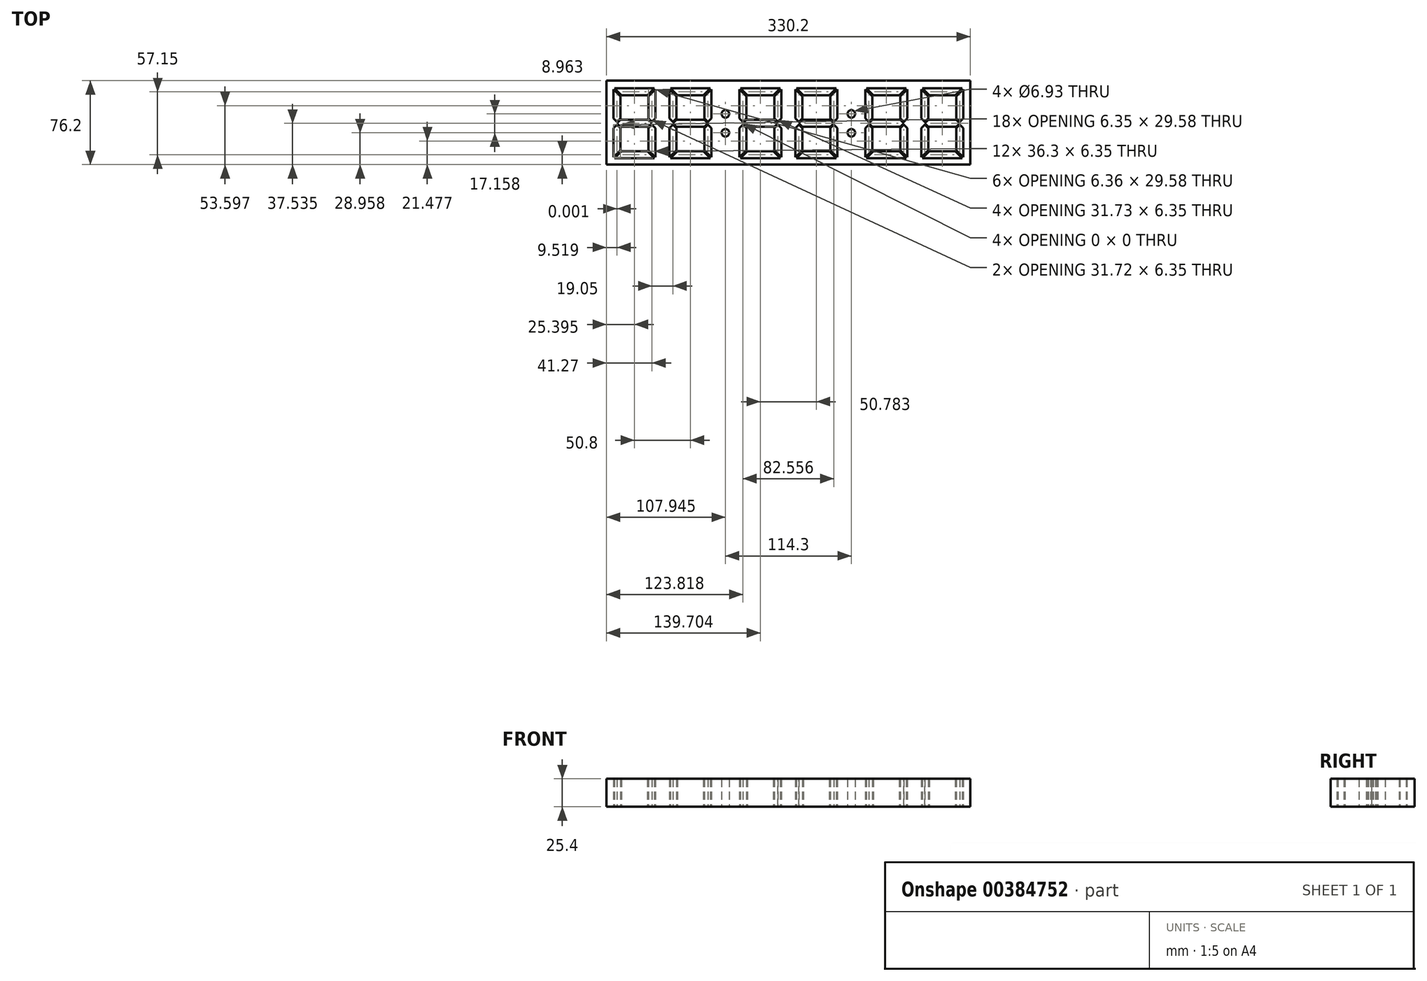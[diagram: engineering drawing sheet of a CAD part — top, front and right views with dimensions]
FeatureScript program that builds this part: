
annotation { "Feature Type Name" : "Feature", "Feature Type Description" : "" }
export const myFeature = defineFeature(function(context is Context, id is Id, definition is map)
    precondition{}
    {
        {
            var Q0;
            Q0=qCreatedBy(makeId("Top.planeOp"),FACE);
            var sketch = newSketch(context, id + "F0", { "sketchPlane" : qUnion([Q0])});
            skLineSegment(sketch, "E0.bottom", {"start": v(-71.32, 52.19) * mm, "end": v(-45.92, 52.19) * mm});
            skLineSegment(sketch, "E1.bottom", {"start": v(-64.08, 45.28) * mm, "end": v(-27.77, 45.28) * mm});
            skLineSegment(sketch, "E1.top", {"start": v(-64.08, -18.22) * mm, "end": v(-27.77, -18.22) * mm});
            skLineSegment(sketch, "E1.left", {"start": v(-64.98, 44.38) * mm, "end": v(-64.98, 18.04) * mm});
            skLineSegment(sketch, "E1.right", {"start": v(-26.87, 44.38) * mm, "end": v(-26.87, 18.04) * mm});
            skLineSegment(sketch, "E2.bottom", {"start": v(-57.73, 38.93) * mm, "end": v(-34.12, 38.93) * mm});
            skLineSegment(sketch, "E2.top", {"start": v(-57.73, -11.87) * mm, "end": v(-34.12, -11.87) * mm});
            skLineSegment(sketch, "E2.left", {"start": v(-58.62, 38.03) * mm, "end": v(-58.62, 17.97) * mm});
            skLineSegment(sketch, "E2.right", {"start": v(-33.22, 38.03) * mm, "end": v(-33.22, 17.97) * mm});
            skLineSegment(sketch, "E3", {"start": v(-45.92, 52.19) * mm, "end": v(-20.52, 52.19) * mm});
            skLineSegment(sketch, "E4", {"start": v(-61.35, 42.55) * mm, "end": v(-57.73, 38.93) * mm});
            skLineSegment(sketch, "E5", {"start": v(-62.25, 41.65) * mm, "end": v(-58.62, 38.03) * mm});
            skLineSegment(sketch, "E6", {"start": v(-62.25, 41.65) * mm, "end": v(-64.98, 44.38) * mm});
            skLineSegment(sketch, "E7", {"start": v(-61.35, 42.55) * mm, "end": v(-64.08, 45.28) * mm});
            skPoint(sketch, "E8.orphan", {"position": v(-64.98, 45.28) * mm});
            skPoint(sketch, "E9.orphan", {"position": v(-58.62, 38.93) * mm});
            skPoint(sketch, "E10.start.orphan", {"position": v(-61.8, 42.1) * mm});
            skLineSegment(sketch, "E11.MirrorCS", {"start": v(-29.6, 41.65) * mm, "end": v(-33.22, 38.03) * mm});
            skLineSegment(sketch, "E12.MirrorCS", {"start": v(-30.5, 42.55) * mm, "end": v(-34.12, 38.93) * mm});
            skPoint(sketch, "E13.MirrorP", {"position": v(-30.05, 42.1) * mm});
            skPoint(sketch, "E14.MirrorP", {"position": v(-26.87, 45.28) * mm});
            skLineSegment(sketch, "E15.MirrorCS", {"start": v(-30.5, 42.55) * mm, "end": v(-27.77, 45.28) * mm});
            skLineSegment(sketch, "E16.MirrorCS", {"start": v(-29.6, 41.65) * mm, "end": v(-26.87, 44.38) * mm});
            skPoint(sketch, "E17.MirrorP", {"position": v(-33.22, 38.93) * mm});
            skLineSegment(sketch, "E18.MirrorCS", {"start": v(-61.35, -15.5) * mm, "end": v(-57.73, -11.87) * mm});
            skPoint(sketch, "E19.MirrorP", {"position": v(-64.97, -18.22) * mm});
            skPoint(sketch, "E20.MirrorP", {"position": v(-61.8, -15.05) * mm});
            skLineSegment(sketch, "E21.MirrorCS", {"start": v(-29.6, -14.6) * mm, "end": v(-26.87, -17.32) * mm});
            skLineSegment(sketch, "E22.MirrorCS", {"start": v(-26.87, -17.32) * mm, "end": v(-26.87, 9) * mm});
            skLineSegment(sketch, "E23.MirrorCS", {"start": v(-29.6, -14.6) * mm, "end": v(-33.22, -10.97) * mm});
            skLineSegment(sketch, "E24.MirrorCS", {"start": v(-62.25, -14.6) * mm, "end": v(-64.98, -17.33) * mm});
            skPoint(sketch, "E25.MirrorP", {"position": v(-30.05, -15.05) * mm});
            skLineSegment(sketch, "E26.MirrorCS", {"start": v(-30.5, -15.5) * mm, "end": v(-27.77, -18.22) * mm});
            skPoint(sketch, "E27.MirrorP", {"position": v(-26.87, -18.22) * mm});
            skLineSegment(sketch, "E28.MirrorCS", {"start": v(-30.5, -15.5) * mm, "end": v(-34.12, -11.87) * mm});
            skPoint(sketch, "E29.MirrorP", {"position": v(-33.22, -11.87) * mm});
            skPoint(sketch, "E30.MirrorP", {"position": v(-58.62, -11.87) * mm});
            skLineSegment(sketch, "E31.MirrorCS", {"start": v(-64.98, -17.33) * mm, "end": v(-64.98, 9.01) * mm});
            skLineSegment(sketch, "E32.MirrorCS", {"start": v(-61.35, -15.5) * mm, "end": v(-64.08, -18.22) * mm});
            skPoint(sketch, "E33.MirrorCS.end.orphan", {"position": v(-42, 45.28) * mm});
            skPoint(sketch, "E33.MirrorCS.start.orphan", {"position": v(-42, 38.93) * mm});
            skPoint(sketch, "E34.end.orphan", {"position": v(-49.84, 45.28) * mm});
            skPoint(sketch, "E34.start.orphan", {"position": v(-49.84, 38.93) * mm});
            skPoint(sketch, "E35.end.orphan", {"position": v(-45.92, -24.57) * mm});
            skPoint(sketch, "E36.MirrorCS.end.orphan", {"position": v(-49.84, -18.22) * mm});
            skPoint(sketch, "E36.MirrorCS.start.orphan", {"position": v(-49.84, -11.87) * mm});
            skPoint(sketch, "E37.MirrorCS.end.orphan", {"position": v(-42, -18.22) * mm});
            skPoint(sketch, "E37.MirrorCS.start.orphan", {"position": v(-42, -11.87) * mm});
            skPoint(sketch, "E38.orphan", {"position": v(-58.62, 12.9) * mm});
            skPoint(sketch, "E39.orphan", {"position": v(-58.62, 14.16) * mm});
            skPoint(sketch, "E40.end.orphan", {"position": v(-64.97, 17.68) * mm});
            skPoint(sketch, "E41.MirrorCS.start.orphan", {"position": v(-58.3, 16.78) * mm});
            skPoint(sketch, "E42.MirrorCS.end.orphan", {"position": v(-64.97, 13.53) * mm});
            skPoint(sketch, "E43.MirrorP", {"position": v(-58.3, 10.28) * mm});
            skPoint(sketch, "E44.end.orphan", {"position": v(-64.98, 13.53) * mm});
            skLineSegment(sketch, "E45.trimOffspring", {"start": v(-64.98, 9.01) * mm, "end": v(-64.98, -17.33) * mm});
            skLineSegment(sketch, "E46.trimOffspring", {"start": v(-58.63, 9.08) * mm, "end": v(-58.63, -10.98) * mm});
            skPoint(sketch, "E47.trimOffspring.start.orphan", {"position": v(-64.97, 16.77) * mm});
            skPoint(sketch, "E48.trimOffspring.end.orphan", {"position": v(-26.87, 13.53) * mm});
            skLineSegment(sketch, "E49.MirrorCS", {"start": v(-26.87, 9) * mm, "end": v(-26.87, -17.32) * mm});
            skPoint(sketch, "E50.MirrorP", {"position": v(-33.54, 10.28) * mm});
            skPoint(sketch, "E51.MirrorP", {"position": v(-33.22, 12.9) * mm});
            skPoint(sketch, "E52.MirrorP", {"position": v(-33.54, 16.78) * mm});
            skLineSegment(sketch, "E53.MirrorCS", {"start": v(-26.87, -17.5) * mm, "end": v(-26.87, 9) * mm});
            skLineSegment(sketch, "E54.MirrorCS", {"start": v(-33.22, 9.08) * mm, "end": v(-33.22, -10.97) * mm});
            skPoint(sketch, "E55.MirrorP", {"position": v(-26.87, 16.77) * mm});
            skPoint(sketch, "E56.MirrorP", {"position": v(-26.87, 17.68) * mm});
            skPoint(sketch, "E57.MirrorP", {"position": v(-33.22, 14.16) * mm});
            skPoint(sketch, "E58.orphan", {"position": v(-64.98, -18.22) * mm});
            skLineSegment(sketch, "E59", {"start": v(-62.25, -14.6) * mm, "end": v(-58.63, -10.98) * mm});
            skLineSegment(sketch, "E60", {"start": v(-58.62, 16.7) * mm, "end": v(-61.78, 13.54) * mm});
            skPoint(sketch, "E61.trimOffspring.end.orphan", {"position": v(-58.62, 13.97) * mm});
            skPoint(sketch, "E62.right.start.orphan", {"position": v(-58.62, 13.53) * mm});
            skPoint(sketch, "E63.trimOffspring.end.orphan", {"position": v(-71.32, 13.8) * mm});
            skPoint(sketch, "E64.orphan", {"position": v(-61.8, 16.7) * mm});
            skLineSegment(sketch, "E65", {"start": v(-61.77, 14.8) * mm, "end": v(-58.62, 17.97) * mm});
            skLineSegment(sketch, "E66.MirrorCS", {"start": v(-61.77, 14.8) * mm, "end": v(-64.9, 17.97) * mm});
            skPoint(sketch, "E67.MirrorP", {"position": v(-61.8, 10.35) * mm});
            skLineSegment(sketch, "E68.MirrorCS", {"start": v(-61.77, 12.25) * mm, "end": v(-58.63, 9.08) * mm});
            skLineSegment(sketch, "E69.MirrorCS", {"start": v(-61.77, 12.25) * mm, "end": v(-64.9, 9.08) * mm});
            skLineSegment(sketch, "E70", {"start": v(-58.62, 16.7) * mm, "end": v(-33.22, 16.7) * mm});
            skLineSegment(sketch, "E71", {"start": v(-58.63, 10.35) * mm, "end": v(-33.23, 10.35) * mm});
            skLineSegment(sketch, "E72", {"start": v(-61.78, 13.54) * mm, "end": v(-58.63, 10.35) * mm});
            skLineSegment(sketch, "E73", {"start": v(-64.9, 17.97) * mm, "end": v(-64.98, 18.04) * mm});
            skPoint(sketch, "E74.orphan", {"position": v(-64.98, 17.1) * mm});
            skPoint(sketch, "E75.end.orphan", {"position": v(-64.97, 16.7) * mm});
            skPoint(sketch, "E76.trimOffspring.end.orphan", {"position": v(-58.63, 9.96) * mm});
            skLineSegment(sketch, "E77", {"start": v(-64.9, 9.08) * mm, "end": v(-64.98, 9.01) * mm});
            skPoint(sketch, "E78.orphan", {"position": v(-64.98, 9.96) * mm});
            skLineSegment(sketch, "E79.MirrorCS", {"start": v(-30.08, 14.8) * mm, "end": v(-33.22, 17.97) * mm});
            skLineSegment(sketch, "E80.MirrorCS", {"start": v(-30.08, 14.8) * mm, "end": v(-26.94, 17.97) * mm});
            skLineSegment(sketch, "E81.MirrorCS", {"start": v(-33.22, 16.7) * mm, "end": v(-30.07, 13.54) * mm});
            skLineSegment(sketch, "E82.MirrorCS", {"start": v(-30.07, 13.54) * mm, "end": v(-33.22, 10.35) * mm});
            skLineSegment(sketch, "E83.MirrorCS", {"start": v(-30.08, 12.26) * mm, "end": v(-33.22, 9.08) * mm});
            skLineSegment(sketch, "E84.MirrorCS", {"start": v(-30.08, 12.26) * mm, "end": v(-26.94, 9.08) * mm});
            skPoint(sketch, "E85.orphan", {"position": v(-33.22, 13.53) * mm});
            skPoint(sketch, "E86.orphan", {"position": v(-33.22, 9.96) * mm});
            skLineSegment(sketch, "E87", {"start": v(-26.94, 9.08) * mm, "end": v(-26.87, 9) * mm});
            skPoint(sketch, "E88.orphan", {"position": v(-33.22, 17.1) * mm});
            skLineSegment(sketch, "E89", {"start": v(-26.94, 17.97) * mm, "end": v(-26.87, 18.04) * mm});
            skPoint(sketch, "E90.end.orphan", {"position": v(-26.87, 16.7) * mm});
            skLineSegment(sketch, "E91.bottom", {"start": v(-20.52, 52.19) * mm, "end": v(-14.17, 52.19) * mm});
            skLineSegment(sketch, "E91.top", {"start": v(-20.52, -24.01) * mm, "end": v(-7.82, -24.01) * mm});
            skLineSegment(sketch, "E92", {"start": v(-14.17, 52.19) * mm, "end": v(-7.82, 52.19) * mm});
            skCircle(sketch, "E93", {"center": v(-14.17, 22.1) * mm, "radius": 3.46 * mm});
            skPoint(sketch, "E94.orphan", {"position": v(-14.17, 52.19) * mm});
            skPoint(sketch, "E95.trimOffspring.end.orphan", {"position": v(-14.17, -24.01) * mm});
            skCircle(sketch, "E96.MirrorC", {"center": v(-14.17, 4.95) * mm, "radius": 3.46 * mm});
            skPoint(sketch, "E97.end.orphan", {"position": v(-7.82, 14.09) * mm});
            skPoint(sketch, "E98.end.orphan", {"position": v(-20.52, -24.57) * mm});
            skPoint(sketch, "E98.start.orphan", {"position": v(-20.52, 13.53) * mm});
            skPoint(sketch, "E99.start.orphan", {"position": v(-20.52, 13.8) * mm});
            skPoint(sketch, "E100.MirrorP", {"position": v(-77.67, 13.53) * mm});
            skPoint(sketch, "E101.MirrorP", {"position": v(-115.77, 13.53) * mm});
            skLineSegment(sketch, "E102.MirrorCS", {"start": v(-77.74, 9.08) * mm, "end": v(-77.67, 9.01) * mm});
            skLineSegment(sketch, "E103.MirrorCS", {"start": v(-115.7, 9.08) * mm, "end": v(-115.78, 9) * mm});
            skLineSegment(sketch, "E104.MirrorCS", {"start": v(-115.7, 17.97) * mm, "end": v(-115.77, 18.04) * mm});
            skLineSegment(sketch, "E105.MirrorCS", {"start": v(-109.42, 16.7) * mm, "end": v(-112.58, 13.54) * mm});
            skLineSegment(sketch, "E106.MirrorCS", {"start": v(-80.87, 13.54) * mm, "end": v(-84.02, 10.35) * mm});
            skLineSegment(sketch, "E107.MirrorCS", {"start": v(-84.03, 16.7) * mm, "end": v(-80.87, 13.54) * mm});
            skLineSegment(sketch, "E108.MirrorCS", {"start": v(-112.58, 13.54) * mm, "end": v(-109.42, 10.35) * mm});
            skLineSegment(sketch, "E109.MirrorCS", {"start": v(-77.74, 17.97) * mm, "end": v(-77.67, 18.04) * mm});
            skLineSegment(sketch, "E110.MirrorCS", {"start": v(-115.78, 9) * mm, "end": v(-115.77, -17.32) * mm});
            skLineSegment(sketch, "E111.MirrorCS", {"start": v(-80.88, 14.8) * mm, "end": v(-84.03, 17.97) * mm});
            skLineSegment(sketch, "E112.MirrorCS", {"start": v(-113.05, -14.6) * mm, "end": v(-115.77, -17.32) * mm});
            skLineSegment(sketch, "E113.MirrorCS", {"start": v(-80.88, 14.8) * mm, "end": v(-77.74, 17.97) * mm});
            skLineSegment(sketch, "E114.MirrorCS", {"start": v(-80.4, -14.6) * mm, "end": v(-77.67, -17.33) * mm});
            skLineSegment(sketch, "E115.MirrorCS", {"start": v(-80.88, 12.25) * mm, "end": v(-84.02, 9.08) * mm});
            skLineSegment(sketch, "E116.MirrorCS", {"start": v(-112.15, -15.5) * mm, "end": v(-114.88, -18.22) * mm});
            skLineSegment(sketch, "E117.MirrorCS", {"start": v(-80.88, 12.25) * mm, "end": v(-77.74, 9.08) * mm});
            skLineSegment(sketch, "E118.MirrorCS", {"start": v(-113.05, 41.65) * mm, "end": v(-115.77, 44.38) * mm});
            skLineSegment(sketch, "E119.MirrorCS", {"start": v(-81.3, -15.5) * mm, "end": v(-78.57, -18.22) * mm});
            skLineSegment(sketch, "E120.MirrorCS", {"start": v(-81.3, 42.55) * mm, "end": v(-78.57, 45.28) * mm});
            skLineSegment(sketch, "E121.MirrorCS", {"start": v(-112.57, 14.8) * mm, "end": v(-115.7, 17.97) * mm});
            skLineSegment(sketch, "E122.MirrorCS", {"start": v(-112.57, 14.8) * mm, "end": v(-109.42, 17.97) * mm});
            skLineSegment(sketch, "E123.MirrorCS", {"start": v(-112.15, 42.55) * mm, "end": v(-114.88, 45.28) * mm});
            skPoint(sketch, "E124.MirrorP", {"position": v(-84.02, 13.53) * mm});
            skLineSegment(sketch, "E125.MirrorCS", {"start": v(-109.42, 9.08) * mm, "end": v(-109.42, -10.97) * mm});
            skPoint(sketch, "E126.MirrorP", {"position": v(-84.02, 12.9) * mm});
            skLineSegment(sketch, "E127.MirrorCS", {"start": v(-109.42, 38.03) * mm, "end": v(-109.42, 17.97) * mm});
            skLineSegment(sketch, "E128.MirrorCS", {"start": v(-112.57, 12.26) * mm, "end": v(-109.42, 9.08) * mm});
            skLineSegment(sketch, "E129.MirrorCS", {"start": v(-115.77, 44.38) * mm, "end": v(-115.77, 18.04) * mm});
            skLineSegment(sketch, "E130.MirrorCS", {"start": v(-112.57, 12.26) * mm, "end": v(-115.7, 9.08) * mm});
            skLineSegment(sketch, "E131.MirrorCS", {"start": v(-80.4, 41.65) * mm, "end": v(-77.67, 44.38) * mm});
            skLineSegment(sketch, "E132.MirrorCS", {"start": v(-112.15, 42.55) * mm, "end": v(-108.53, 38.93) * mm});
            skPoint(sketch, "E133.MirrorP", {"position": v(-109.1, 16.78) * mm});
            skPoint(sketch, "E134.MirrorP", {"position": v(-109.1, 10.28) * mm});
            skPoint(sketch, "E135.MirrorP", {"position": v(-109.42, 12.9) * mm});
            skLineSegment(sketch, "E136.MirrorCS", {"start": v(-113.05, -14.6) * mm, "end": v(-109.42, -10.97) * mm});
            skPoint(sketch, "E137.MirrorP", {"position": v(-115.77, -18.22) * mm});
            skLineSegment(sketch, "E138.MirrorCS", {"start": v(-81.3, -15.5) * mm, "end": v(-84.92, -11.87) * mm});
            skLineSegment(sketch, "E139.MirrorCS", {"start": v(-81.3, 42.55) * mm, "end": v(-84.92, 38.93) * mm});
            skLineSegment(sketch, "E140.MirrorCS", {"start": v(-80.4, -14.6) * mm, "end": v(-84.02, -10.98) * mm});
            skPoint(sketch, "E141.MirrorP", {"position": v(-115.77, 45.28) * mm});
            skLineSegment(sketch, "E142.MirrorCS", {"start": v(-84.92, -11.87) * mm, "end": v(-108.53, -11.87) * mm});
            skPoint(sketch, "E143.MirrorP", {"position": v(-109.42, 13.53) * mm});
            skLineSegment(sketch, "E144.MirrorCS", {"start": v(-77.67, -17.33) * mm, "end": v(-77.67, 9.01) * mm});
            skPoint(sketch, "E145.MirrorP", {"position": v(-77.67, 16.77) * mm});
            skLineSegment(sketch, "E146.MirrorCS", {"start": v(-113.05, 41.65) * mm, "end": v(-109.42, 38.03) * mm});
            skPoint(sketch, "E147.MirrorP", {"position": v(-109.42, 14.16) * mm});
            skPoint(sketch, "E148.MirrorP", {"position": v(-122.12, 13.53) * mm});
            skPoint(sketch, "E149.MirrorP", {"position": v(-77.67, -18.22) * mm});
            skLineSegment(sketch, "E150.MirrorCS", {"start": v(-78.57, -18.22) * mm, "end": v(-114.88, -18.22) * mm});
            skPoint(sketch, "E151.MirrorP", {"position": v(-84.34, 16.78) * mm});
            skLineSegment(sketch, "E152.MirrorCS", {"start": v(-112.15, -15.5) * mm, "end": v(-108.53, -11.87) * mm});
            skPoint(sketch, "E153.MirrorP", {"position": v(-84.34, 10.28) * mm});
            skPoint(sketch, "E154.MirrorP", {"position": v(-84.03, 14.16) * mm});
            skLineSegment(sketch, "E155.MirrorCS", {"start": v(-115.77, -17.5) * mm, "end": v(-115.78, 9) * mm});
            skPoint(sketch, "E156.MirrorP", {"position": v(-115.78, 16.7) * mm});
            skLineSegment(sketch, "E157.MirrorCS", {"start": v(-80.4, 41.65) * mm, "end": v(-84.03, 38.03) * mm});
            skPoint(sketch, "E158.MirrorP", {"position": v(-84.02, 13.97) * mm});
            skLineSegment(sketch, "E159.MirrorCS", {"start": v(-115.77, -17.32) * mm, "end": v(-115.78, 9) * mm});
            skPoint(sketch, "E160.MirrorP", {"position": v(-109.42, -11.87) * mm});
            skPoint(sketch, "E161.MirrorP", {"position": v(-77.67, 45.28) * mm});
            skPoint(sketch, "E162.MirrorP", {"position": v(-77.68, 16.7) * mm});
            skPoint(sketch, "E163.MirrorP", {"position": v(-77.67, 9.96) * mm});
            skPoint(sketch, "E164.MirrorP", {"position": v(-92.8, -11.87) * mm});
            skPoint(sketch, "E165.MirrorP", {"position": v(-80.85, 42.1) * mm});
            skLineSegment(sketch, "E166.MirrorCS", {"start": v(-84.02, 9.08) * mm, "end": v(-84.02, -10.98) * mm});
            skPoint(sketch, "E167.MirrorP", {"position": v(-92.8, -18.22) * mm});
            skLineSegment(sketch, "E168.MirrorCS", {"start": v(-77.67, 9.01) * mm, "end": v(-77.67, -17.33) * mm});
            skPoint(sketch, "E169.MirrorP", {"position": v(-84.02, -11.87) * mm});
            skPoint(sketch, "E170.MirrorP", {"position": v(-100.64, 45.28) * mm});
            skPoint(sketch, "E171.MirrorP", {"position": v(-84.03, 38.93) * mm});
            skPoint(sketch, "E172.MirrorP", {"position": v(-84.02, 9.96) * mm});
            skPoint(sketch, "E173.MirrorP", {"position": v(-109.42, 9.96) * mm});
            skPoint(sketch, "E174.MirrorP", {"position": v(-109.42, 17.1) * mm});
            skPoint(sketch, "E175.MirrorP", {"position": v(-115.78, 16.77) * mm});
            skLineSegment(sketch, "E176.MirrorCS", {"start": v(-84.92, 38.93) * mm, "end": v(-108.53, 38.93) * mm});
            skPoint(sketch, "E177.MirrorP", {"position": v(-100.64, -18.22) * mm});
            skPoint(sketch, "E178.MirrorP", {"position": v(-115.77, 17.68) * mm});
            skPoint(sketch, "E179.MirrorP", {"position": v(-100.64, 38.93) * mm});
            skPoint(sketch, "E180.MirrorP", {"position": v(-80.85, 10.35) * mm});
            skPoint(sketch, "E181.MirrorP", {"position": v(-100.64, -11.87) * mm});
            skPoint(sketch, "E182.MirrorP", {"position": v(-92.8, 38.93) * mm});
            skPoint(sketch, "E183.MirrorP", {"position": v(-109.42, 38.93) * mm});
            skLineSegment(sketch, "E184.MirrorCS", {"start": v(-77.67, 44.38) * mm, "end": v(-77.67, 18.04) * mm});
            skPoint(sketch, "E185.MirrorP", {"position": v(-77.67, 17.1) * mm});
            skPoint(sketch, "E186.MirrorP", {"position": v(-112.6, 42.1) * mm});
            skLineSegment(sketch, "E187.MirrorCS", {"start": v(-84.03, 16.7) * mm, "end": v(-109.43, 16.7) * mm});
            skLineSegment(sketch, "E188.MirrorCS", {"start": v(-84.02, 10.35) * mm, "end": v(-109.42, 10.35) * mm});
            skLineSegment(sketch, "E189.MirrorCS", {"start": v(-84.03, 38.03) * mm, "end": v(-84.03, 17.97) * mm});
            skPoint(sketch, "E190.MirrorP", {"position": v(-112.6, -15.05) * mm});
            skPoint(sketch, "E191.MirrorP", {"position": v(-80.85, 16.7) * mm});
            skPoint(sketch, "E192.MirrorP", {"position": v(-77.67, 17.68) * mm});
            skPoint(sketch, "E193.MirrorP", {"position": v(-92.8, 45.28) * mm});
            skPoint(sketch, "E194.MirrorP", {"position": v(-80.85, -15.05) * mm});
            skPoint(sketch, "E195.MirrorP", {"position": v(-122.13, 13.8) * mm});
            skLineSegment(sketch, "E196.MirrorCS", {"start": v(-78.57, 45.28) * mm, "end": v(-114.88, 45.28) * mm});
            skLineSegment(sketch, "E197.bottom", {"start": v(-71.32, 52.19) * mm, "end": v(-122.12, 52.19) * mm});
            skLineSegment(sketch, "E197.top", {"start": v(-71.32, -24.01) * mm, "end": v(-122.12, -24.01) * mm});
            skLineSegment(sketch, "E197.right", {"start": v(-122.12, 52.19) * mm, "end": v(-122.12, -24.01) * mm});
            skLineSegment(sketch, "E198", {"start": v(-20.52, -24.01) * mm, "end": v(-71.32, -24.01) * mm});
            skPoint(sketch, "E199.orphan", {"position": v(-71.32, -24.57) * mm});
            skPoint(sketch, "E200.MirrorCS.start.orphan", {"position": v(-20.52, 51.63) * mm});
            skPoint(sketch, "E201.1.0.0", {"position": v(-7.83, 13.8) * mm});
            skLineSegment(sketch, "E201.1.0.1", {"start": v(93.78, 52.19) * mm, "end": v(100.13, 52.19) * mm});
            skLineSegment(sketch, "E201.1.0.2", {"start": v(30.28, 9.08) * mm, "end": v(30.28, -10.98) * mm});
            skLineSegment(sketch, "E201.1.0.3", {"start": v(30.27, 16.7) * mm, "end": v(4.87, 16.7) * mm});
            skPoint(sketch, "E201.1.0.4", {"position": v(81.08, -11.87) * mm});
            skLineSegment(sketch, "E201.1.0.5", {"start": v(93.78, -24.01) * mm, "end": v(106.48, -24.01) * mm});
            skPoint(sketch, "E201.1.0.6", {"position": v(72.3, -11.87) * mm});
            skPoint(sketch, "E201.1.0.7", {"position": v(52.5, -15.05) * mm});
            skPoint(sketch, "E201.1.0.8", {"position": v(33.45, 10.35) * mm});
            skLineSegment(sketch, "E201.1.0.9", {"start": v(35.73, 45.28) * mm, "end": v(-0.58, 45.28) * mm});
            skLineSegment(sketch, "E201.1.0.10", {"start": v(-1.47, 44.38) * mm, "end": v(-1.47, 18.04) * mm});
            skPoint(sketch, "E201.1.0.11", {"position": v(21.5, -18.22) * mm});
            skPoint(sketch, "E201.1.0.12", {"position": v(36.63, 9.96) * mm});
            skPoint(sketch, "E201.1.0.13", {"position": v(49.32, 9.96) * mm});
            skPoint(sketch, "E201.1.0.14", {"position": v(84.25, -15.05) * mm});
            skLineSegment(sketch, "E201.1.0.15", {"start": v(55.67, 10.35) * mm, "end": v(81.07, 10.35) * mm});
            skPoint(sketch, "E201.1.0.16", {"position": v(81.08, 38.93) * mm});
            skPoint(sketch, "E201.1.0.17", {"position": v(87.43, 45.28) * mm});
            skCircle(sketch, "E201.1.0.18", {"center": v(100.13, 4.95) * mm, "radius": 3.46 * mm});
            skPoint(sketch, "E201.1.0.19", {"position": v(42.98, -24.57) * mm});
            skLineSegment(sketch, "E201.1.0.20", {"start": v(81.08, 9.08) * mm, "end": v(81.08, -10.97) * mm});
            skPoint(sketch, "E201.1.0.21", {"position": v(33.45, -15.05) * mm});
            skPoint(sketch, "E201.1.0.22", {"position": v(29.96, 16.78) * mm});
            skPoint(sketch, "E201.1.0.23", {"position": v(81.08, 17.1) * mm});
            skPoint(sketch, "E201.1.0.25", {"position": v(49.33, 17.68) * mm});
            skPoint(sketch, "E201.1.0.26", {"position": v(72.3, 38.93) * mm});
            skLineSegment(sketch, "E201.1.0.27", {"start": v(29.38, 38.93) * mm, "end": v(5.77, 38.93) * mm});
            skPoint(sketch, "E201.1.0.28", {"position": v(81.08, 9.96) * mm});
            skLineSegment(sketch, "E201.1.0.29", {"start": v(4.88, 9.08) * mm, "end": v(4.88, -10.97) * mm});
            skPoint(sketch, "E201.1.0.30", {"position": v(55.68, 13.97) * mm});
            skPoint(sketch, "E201.1.0.31", {"position": v(-1.47, 17.68) * mm});
            skPoint(sketch, "E201.1.0.32", {"position": v(13.66, 38.93) * mm});
            skLineSegment(sketch, "E201.1.0.34", {"start": v(56.57, 38.93) * mm, "end": v(80.18, 38.93) * mm});
            skLineSegment(sketch, "E201.1.0.35", {"start": v(49.32, 44.38) * mm, "end": v(49.32, 18.04) * mm});
            skLineSegment(sketch, "E201.1.0.36", {"start": v(42.98, 52.19) * mm, "end": v(68.38, 52.19) * mm});
            skLineSegment(sketch, "E201.1.0.37", {"start": v(42.98, -24.01) * mm, "end": v(-7.82, -24.01) * mm});
            skPoint(sketch, "E201.1.0.38", {"position": v(36.63, -18.22) * mm});
            skPoint(sketch, "E201.1.0.39", {"position": v(30.28, 12.9) * mm});
            skPoint(sketch, "E201.1.0.40", {"position": v(87.43, 16.77) * mm});
            skPoint(sketch, "E201.1.0.41", {"position": v(30.27, 14.16) * mm});
            skPoint(sketch, "E201.1.0.42", {"position": v(13.66, 45.28) * mm});
            skPoint(sketch, "E201.1.0.43", {"position": v(-1.47, 13.53) * mm});
            skPoint(sketch, "E201.1.0.44", {"position": v(64.46, -11.87) * mm});
            skPoint(sketch, "E201.1.0.45", {"position": v(52.5, 42.1) * mm});
            skLineSegment(sketch, "E201.1.0.46", {"start": v(55.67, 9.08) * mm, "end": v(55.67, -10.98) * mm});
            skPoint(sketch, "E201.1.0.47", {"position": v(33.45, 16.7) * mm});
            skPoint(sketch, "E201.1.0.48", {"position": v(-1.47, 45.28) * mm});
            skLineSegment(sketch, "E201.1.0.49", {"start": v(93.78, -24.01) * mm, "end": v(42.98, -24.01) * mm});
            skPoint(sketch, "E201.1.0.50", {"position": v(49.32, 45.28) * mm});
            skPoint(sketch, "E201.1.0.51", {"position": v(56, 10.28) * mm});
            skLineSegment(sketch, "E201.1.0.52", {"start": v(55.68, 38.03) * mm, "end": v(55.68, 17.97) * mm});
            skLineSegment(sketch, "E201.1.0.53", {"start": v(42.98, 52.19) * mm, "end": v(-7.82, 52.19) * mm});
            skPoint(sketch, "E201.1.0.54", {"position": v(93.78, 13.8) * mm});
            skPoint(sketch, "E201.1.0.55", {"position": v(87.43, 13.53) * mm});
            skPoint(sketch, "E201.1.0.56", {"position": v(64.46, 45.28) * mm});
            skPoint(sketch, "E201.1.0.57", {"position": v(5.2, 16.78) * mm});
            skPoint(sketch, "E201.1.0.58", {"position": v(80.76, 10.28) * mm});
            skPoint(sketch, "E201.1.0.59", {"position": v(55.67, 9.96) * mm});
            skPoint(sketch, "E201.1.0.60", {"position": v(72.3, 45.28) * mm});
            skPoint(sketch, "E201.1.0.61", {"position": v(49.32, -18.22) * mm});
            skPoint(sketch, "E201.1.0.62", {"position": v(42.98, 13.8) * mm});
            skPoint(sketch, "E201.1.0.63", {"position": v(55.68, 13.53) * mm});
            skPoint(sketch, "E201.1.0.64", {"position": v(55.68, -11.87) * mm});
            skPoint(sketch, "E201.1.0.65", {"position": v(106.48, 14.09) * mm});
            skPoint(sketch, "E201.1.0.66", {"position": v(93.78, 13.53) * mm});
            skLineSegment(sketch, "E201.1.0.67", {"start": v(100.13, 52.19) * mm, "end": v(106.48, 52.19) * mm});
            skPoint(sketch, "E201.1.0.68", {"position": v(4.88, 12.9) * mm});
            skPoint(sketch, "E201.1.0.69", {"position": v(49.32, 13.53) * mm});
            skPoint(sketch, "E201.1.0.70", {"position": v(100.13, 52.19) * mm});
            skPoint(sketch, "E201.1.0.71", {"position": v(30.28, -11.87) * mm});
            skPoint(sketch, "E201.1.0.72", {"position": v(1.7, -15.05) * mm});
            skLineSegment(sketch, "E201.1.0.73", {"start": v(87.43, 44.38) * mm, "end": v(87.43, 18.04) * mm});
            skPoint(sketch, "E201.1.0.74", {"position": v(68.38, -24.57) * mm});
            skPoint(sketch, "E201.1.0.75", {"position": v(55.68, 12.9) * mm});
            skPoint(sketch, "E201.1.0.76", {"position": v(49.32, 17.1) * mm});
            skPoint(sketch, "E201.1.0.77", {"position": v(4.88, -11.87) * mm});
            skLineSegment(sketch, "E201.1.0.78", {"start": v(49.32, 9.01) * mm, "end": v(49.32, -17.33) * mm});
            skPoint(sketch, "E201.1.0.79", {"position": v(64.46, 38.93) * mm});
            skLineSegment(sketch, "E201.1.0.80", {"start": v(56.57, -11.87) * mm, "end": v(80.18, -11.87) * mm});
            skLineSegment(sketch, "E201.1.0.81", {"start": v(4.88, 38.03) * mm, "end": v(4.88, 17.97) * mm});
            skPoint(sketch, "E201.1.0.82", {"position": v(1.7, 42.1) * mm});
            skPoint(sketch, "E201.1.0.83", {"position": v(52.5, 10.35) * mm});
            skPoint(sketch, "E201.1.0.84", {"position": v(49.33, 16.7) * mm});
            skPoint(sketch, "E201.1.0.85", {"position": v(36.63, 17.68) * mm});
            skPoint(sketch, "E201.1.0.86", {"position": v(64.46, -18.22) * mm});
            skPoint(sketch, "E201.1.0.87", {"position": v(81.08, 12.9) * mm});
            skPoint(sketch, "E201.1.0.88", {"position": v(55.68, 38.93) * mm});
            skPoint(sketch, "E201.1.0.89", {"position": v(5.2, 10.28) * mm});
            skPoint(sketch, "E201.1.0.90", {"position": v(36.63, 13.53) * mm});
            skPoint(sketch, "E201.1.0.91", {"position": v(93.78, -24.57) * mm});
            skLineSegment(sketch, "E201.1.0.92", {"start": v(50.22, 45.28) * mm, "end": v(86.53, 45.28) * mm});
            skLineSegment(sketch, "E201.1.0.93", {"start": v(50.22, -18.22) * mm, "end": v(86.53, -18.22) * mm});
            skPoint(sketch, "E201.1.0.94", {"position": v(30.28, 9.96) * mm});
            skPoint(sketch, "E201.1.0.95", {"position": v(29.96, 10.28) * mm});
            skLineSegment(sketch, "E201.1.0.96", {"start": v(30.27, 38.03) * mm, "end": v(30.27, 17.97) * mm});
            skLineSegment(sketch, "E201.1.0.97", {"start": v(30.28, 10.35) * mm, "end": v(4.88, 10.35) * mm});
            skPoint(sketch, "E201.1.0.98", {"position": v(87.43, -18.22) * mm});
            skPoint(sketch, "E201.1.0.99", {"position": v(52.5, 16.7) * mm});
            skPoint(sketch, "E201.1.0.100", {"position": v(30.27, 38.93) * mm});
            skLineSegment(sketch, "E201.1.0.101", {"start": v(-1.47, -17.32) * mm, "end": v(-1.48, 9) * mm});
            skPoint(sketch, "E201.1.0.102", {"position": v(36.63, 45.28) * mm});
            skPoint(sketch, "E201.1.0.103", {"position": v(4.88, 17.1) * mm});
            skPoint(sketch, "E201.1.0.104", {"position": v(4.88, 9.96) * mm});
            skLineSegment(sketch, "E201.1.0.105", {"start": v(68.38, 52.19) * mm, "end": v(93.78, 52.19) * mm});
            skLineSegment(sketch, "E201.1.0.106", {"start": v(29.38, -11.87) * mm, "end": v(5.77, -11.87) * mm});
            skPoint(sketch, "E201.1.0.107", {"position": v(13.66, -11.87) * mm});
            skPoint(sketch, "E201.1.0.108", {"position": v(93.78, 51.63) * mm});
            skPoint(sketch, "E201.1.0.109", {"position": v(-7.82, 13.53) * mm});
            skLineSegment(sketch, "E201.1.0.110", {"start": v(35.73, -18.22) * mm, "end": v(-0.58, -18.22) * mm});
            skPoint(sketch, "E201.1.0.111", {"position": v(4.88, 38.93) * mm});
            skPoint(sketch, "E201.1.0.112", {"position": v(21.5, -11.87) * mm});
            skLineSegment(sketch, "E201.1.0.113", {"start": v(36.63, 44.38) * mm, "end": v(36.63, 18.04) * mm});
            skCircle(sketch, "E201.1.0.114", {"center": v(100.13, 22.1) * mm, "radius": 3.46 * mm});
            skPoint(sketch, "E201.1.0.115", {"position": v(21.5, 45.28) * mm});
            skLineSegment(sketch, "E201.1.0.116", {"start": v(36.63, -17.33) * mm, "end": v(36.63, 9.01) * mm});
            skPoint(sketch, "E201.1.0.117", {"position": v(21.5, 38.93) * mm});
            skLineSegment(sketch, "E201.1.0.118", {"start": v(55.68, 16.7) * mm, "end": v(81.08, 16.7) * mm});
            skPoint(sketch, "E201.1.0.119", {"position": v(13.66, -18.22) * mm});
            skPoint(sketch, "E201.1.0.120", {"position": v(33.45, 42.1) * mm});
            skPoint(sketch, "E201.1.0.121", {"position": v(84.25, 42.1) * mm});
            skPoint(sketch, "E201.1.0.122", {"position": v(72.3, -18.22) * mm});
            skPoint(sketch, "E201.1.0.123", {"position": v(56, 16.78) * mm});
            skPoint(sketch, "E201.1.0.124", {"position": v(100.13, -24.01) * mm});
            skPoint(sketch, "E201.1.0.125", {"position": v(80.76, 16.78) * mm});
            skPoint(sketch, "E201.1.0.126", {"position": v(-1.47, -18.22) * mm});
            skLineSegment(sketch, "E201.1.0.127", {"start": v(81.08, 38.03) * mm, "end": v(81.08, 17.97) * mm});
            skPoint(sketch, "E201.1.0.128", {"position": v(-1.48, 16.77) * mm});
            skLineSegment(sketch, "E201.1.0.129", {"start": v(87.43, -17.5) * mm, "end": v(87.43, 9) * mm});
            skPoint(sketch, "E201.1.0.130", {"position": v(36.62, 16.7) * mm});
            skLineSegment(sketch, "E201.1.0.131", {"start": v(56.57, -11.87) * mm, "end": v(80.18, -11.87) * mm});
            skLineSegment(sketch, "E201.1.0.132", {"start": v(4.88, 9.08) * mm, "end": v(4.88, -10.97) * mm});
            skPoint(sketch, "E201.1.0.133", {"position": v(55.68, 14.16) * mm});
            skPoint(sketch, "E201.1.0.134", {"position": v(49.33, -18.22) * mm});
            skPoint(sketch, "E201.1.0.135", {"position": v(4.88, 12.9) * mm});
            skPoint(sketch, "E201.1.0.136", {"position": v(36.63, 17.1) * mm});
            skLineSegment(sketch, "E201.1.0.137", {"start": v(81.08, 9.08) * mm, "end": v(81.08, -10.97) * mm});
            skLineSegment(sketch, "E201.1.0.138", {"start": v(36.63, 9.01) * mm, "end": v(36.63, -17.33) * mm});
            skLineSegment(sketch, "E201.1.0.139", {"start": v(33, 42.55) * mm, "end": v(29.38, 38.93) * mm});
            skPoint(sketch, "E201.1.0.140", {"position": v(-1.47, 45.28) * mm});
            skLineSegment(sketch, "E201.1.0.141", {"start": v(52.05, -14.6) * mm, "end": v(55.67, -10.98) * mm});
            skLineSegment(sketch, "E201.1.0.142", {"start": v(1.25, 41.65) * mm, "end": v(4.88, 38.03) * mm});
            skLineSegment(sketch, "E201.1.0.143", {"start": v(84.7, -14.6) * mm, "end": v(81.08, -10.97) * mm});
            skLineSegment(sketch, "E201.1.0.144", {"start": v(52.95, -15.5) * mm, "end": v(56.57, -11.87) * mm});
            skPoint(sketch, "E201.1.0.145", {"position": v(5.2, 10.28) * mm});
            skPoint(sketch, "E201.1.0.146", {"position": v(81.08, 14.16) * mm});
            skPoint(sketch, "E201.1.0.147", {"position": v(56, 10.28) * mm});
            skPoint(sketch, "E201.1.0.148", {"position": v(49.33, 16.77) * mm});
            skPoint(sketch, "E201.1.0.149", {"position": v(87.43, 45.28) * mm});
            skPoint(sketch, "E201.1.0.150", {"position": v(87.43, 13.53) * mm});
            skPoint(sketch, "E201.1.0.151", {"position": v(55.68, 12.9) * mm});
            skPoint(sketch, "E201.1.0.152", {"position": v(93.78, -24.57) * mm});
            skPoint(sketch, "E201.1.0.153", {"position": v(4.88, 14.16) * mm});
            skLineSegment(sketch, "E201.1.0.154", {"start": v(33.9, -14.6) * mm, "end": v(30.28, -10.98) * mm});
            skLineSegment(sketch, "E201.1.0.155", {"start": v(29.38, -11.87) * mm, "end": v(5.77, -11.87) * mm});
            skPoint(sketch, "E201.1.0.156", {"position": v(87.43, -18.22) * mm});
            skPoint(sketch, "E201.1.0.157", {"position": v(5.2, 16.78) * mm});
            skPoint(sketch, "E201.1.0.158", {"position": v(87.43, 16.7) * mm});
            skLineSegment(sketch, "E201.1.0.159", {"start": v(33, -15.5) * mm, "end": v(29.38, -11.87) * mm});
            skLineSegment(sketch, "E201.1.0.160", {"start": v(83.8, -15.5) * mm, "end": v(80.18, -11.87) * mm});
            skLineSegment(sketch, "E201.1.0.161", {"start": v(-1.48, 9) * mm, "end": v(-1.47, -17.32) * mm});
            skLineSegment(sketch, "E201.1.0.162", {"start": v(52.95, 42.55) * mm, "end": v(56.57, 38.93) * mm});
            skLineSegment(sketch, "E201.1.0.163", {"start": v(87.43, 44.38) * mm, "end": v(87.43, 18.04) * mm});
            skLineSegment(sketch, "E201.1.0.164", {"start": v(33.9, 41.65) * mm, "end": v(30.27, 38.03) * mm});
            skPoint(sketch, "E201.1.0.165", {"position": v(49.33, 13.53) * mm});
            skLineSegment(sketch, "E201.1.0.166", {"start": v(83.8, 42.55) * mm, "end": v(80.18, 38.93) * mm});
            skLineSegment(sketch, "E201.1.0.167", {"start": v(52.05, 41.65) * mm, "end": v(55.68, 38.03) * mm});
            skLineSegment(sketch, "E201.1.0.168", {"start": v(4.88, 38.03) * mm, "end": v(4.88, 17.97) * mm});
            skPoint(sketch, "E201.1.0.169", {"position": v(80.76, 16.78) * mm});
            skLineSegment(sketch, "E201.1.0.170", {"start": v(87.43, 9) * mm, "end": v(87.43, -17.32) * mm});
            skLineSegment(sketch, "E201.1.0.171", {"start": v(50.22, -18.22) * mm, "end": v(86.53, -18.22) * mm});
            skPoint(sketch, "E201.1.0.172", {"position": v(-1.47, 13.53) * mm});
            skLineSegment(sketch, "E201.1.0.173", {"start": v(-1.47, 44.38) * mm, "end": v(-1.47, 18.04) * mm});
            skPoint(sketch, "E201.1.0.174", {"position": v(81.08, 12.9) * mm});
            skLineSegment(sketch, "E201.1.0.175", {"start": v(84.7, 41.65) * mm, "end": v(81.08, 38.03) * mm});
            skPoint(sketch, "E201.1.0.176", {"position": v(30.28, 13.97) * mm});
            skPoint(sketch, "E201.1.0.177", {"position": v(80.76, 10.28) * mm});
            skPoint(sketch, "E201.1.0.178", {"position": v(30.28, 12.9) * mm});
            skLineSegment(sketch, "E201.1.0.179", {"start": v(2.15, -15.5) * mm, "end": v(5.77, -11.87) * mm});
            skPoint(sketch, "E201.1.0.180", {"position": v(29.96, 10.28) * mm});
            skPoint(sketch, "E201.1.0.181", {"position": v(-1.48, 16.7) * mm});
            skLineSegment(sketch, "E201.1.0.182", {"start": v(2.15, 42.55) * mm, "end": v(5.77, 38.93) * mm});
            skPoint(sketch, "E201.1.0.183", {"position": v(36.63, 13.53) * mm});
            skLineSegment(sketch, "E201.1.0.184", {"start": v(81.08, 38.03) * mm, "end": v(81.08, 17.97) * mm});
            skPoint(sketch, "E201.1.0.185", {"position": v(56, 16.78) * mm});
            skLineSegment(sketch, "E201.1.0.186", {"start": v(49.32, -17.33) * mm, "end": v(49.32, 9.01) * mm});
            skLineSegment(sketch, "E201.1.0.187", {"start": v(1.25, -14.6) * mm, "end": v(4.88, -10.97) * mm});
            skLineSegment(sketch, "E201.1.0.188", {"start": v(35.73, -18.22) * mm, "end": v(-0.58, -18.22) * mm});
            skPoint(sketch, "E201.1.0.189", {"position": v(29.96, 16.78) * mm});
            skPoint(sketch, "E201.1.0.190", {"position": v(87.43, 17.68) * mm});
            skPoint(sketch, "E201.1.0.191", {"position": v(-1.47, -18.22) * mm});
            skPoint(sketch, "E201.1.0.192", {"position": v(36.63, -18.22) * mm});
            skLineSegment(sketch, "E201.1.0.193", {"start": v(87.43, 44.38) * mm, "end": v(87.43, 18.04) * mm});
            skLineSegment(sketch, "E201.1.0.194", {"start": v(33, 42.55) * mm, "end": v(35.73, 45.28) * mm});
            skPoint(sketch, "E201.1.0.195", {"position": v(4.88, 13.53) * mm});
            skPoint(sketch, "E201.1.0.196", {"position": v(30.28, 13.53) * mm});
            skLineSegment(sketch, "E201.1.0.197", {"start": v(1.73, 14.8) * mm, "end": v(-1.4, 17.97) * mm});
            skLineSegment(sketch, "E201.1.0.198", {"start": v(1.73, 12.26) * mm, "end": v(4.88, 9.08) * mm});
            skPoint(sketch, "E201.1.0.199", {"position": v(36.63, 16.77) * mm});
            skLineSegment(sketch, "E201.1.0.200", {"start": v(81.08, 38.03) * mm, "end": v(81.08, 17.97) * mm});
            skLineSegment(sketch, "E201.1.0.201", {"start": v(4.88, 9.08) * mm, "end": v(4.88, -10.97) * mm});
            skLineSegment(sketch, "E201.1.0.202", {"start": v(33.9, 41.65) * mm, "end": v(36.63, 44.38) * mm});
            skLineSegment(sketch, "E201.1.0.203", {"start": v(1.73, 12.26) * mm, "end": v(-1.4, 9.08) * mm});
            skPoint(sketch, "E201.1.0.204", {"position": v(-1.47, 13.53) * mm});
            skPoint(sketch, "E201.1.0.205", {"position": v(49.33, 13.53) * mm});
            skLineSegment(sketch, "E201.1.0.206", {"start": v(4.88, 38.03) * mm, "end": v(4.88, 17.97) * mm});
            skLineSegment(sketch, "E201.1.0.207", {"start": v(-1.47, 44.38) * mm, "end": v(-1.47, 18.04) * mm});
            skLineSegment(sketch, "E201.1.0.208", {"start": v(52.05, 41.65) * mm, "end": v(49.32, 44.38) * mm});
            skLineSegment(sketch, "E201.1.0.209", {"start": v(52.95, 42.55) * mm, "end": v(50.22, 45.28) * mm});
            skPoint(sketch, "E201.1.0.210", {"position": v(36.63, 13.53) * mm});
            skLineSegment(sketch, "E201.1.0.211", {"start": v(84.22, 12.26) * mm, "end": v(81.08, 9.08) * mm});
            skLineSegment(sketch, "E201.1.0.212", {"start": v(52.53, 12.25) * mm, "end": v(55.67, 9.08) * mm});
            skLineSegment(sketch, "E201.1.0.213", {"start": v(1.73, 14.8) * mm, "end": v(4.88, 17.97) * mm});
            skLineSegment(sketch, "E201.1.0.214", {"start": v(-1.47, -17.5) * mm, "end": v(-1.48, 9) * mm});
            skLineSegment(sketch, "E201.1.0.215", {"start": v(81.08, 9.08) * mm, "end": v(81.08, -10.97) * mm});
            skLineSegment(sketch, "E201.1.0.216", {"start": v(87.43, 9) * mm, "end": v(87.43, -17.32) * mm});
            skPoint(sketch, "E201.1.0.217", {"position": v(81.08, 13.53) * mm});
            skPoint(sketch, "E201.1.0.218", {"position": v(87.43, 13.53) * mm});
            skLineSegment(sketch, "E201.1.0.219", {"start": v(84.22, 12.26) * mm, "end": v(87.36, 9.08) * mm});
            skLineSegment(sketch, "E201.1.0.220", {"start": v(52.53, 12.25) * mm, "end": v(49.4, 9.08) * mm});
            skLineSegment(sketch, "E201.1.0.221", {"start": v(84.7, -14.6) * mm, "end": v(87.43, -17.32) * mm});
            skLineSegment(sketch, "E201.1.0.222", {"start": v(33, -15.5) * mm, "end": v(35.73, -18.22) * mm});
            skLineSegment(sketch, "E201.1.0.223", {"start": v(1.25, 41.65) * mm, "end": v(-1.47, 44.38) * mm});
            skPoint(sketch, "E201.1.0.224", {"position": v(36.63, 13.53) * mm});
            skLineSegment(sketch, "E201.1.0.225", {"start": v(84.22, 14.8) * mm, "end": v(81.08, 17.97) * mm});
            skLineSegment(sketch, "E201.1.0.226", {"start": v(33.9, -14.6) * mm, "end": v(36.63, -17.33) * mm});
            skPoint(sketch, "E201.1.0.227", {"position": v(-1.47, 13.53) * mm});
            skLineSegment(sketch, "E201.1.0.228", {"start": v(52.53, 14.8) * mm, "end": v(49.4, 17.97) * mm});
            skLineSegment(sketch, "E201.1.0.229", {"start": v(52.53, 14.8) * mm, "end": v(55.68, 17.97) * mm});
            skLineSegment(sketch, "E201.1.0.230", {"start": v(33.42, 14.8) * mm, "end": v(36.56, 17.97) * mm});
            skLineSegment(sketch, "E201.1.0.231", {"start": v(84.22, 14.8) * mm, "end": v(87.36, 17.97) * mm});
            skLineSegment(sketch, "E201.1.0.232", {"start": v(52.95, -15.5) * mm, "end": v(50.22, -18.22) * mm});
            skPoint(sketch, "E201.1.0.233", {"position": v(49.33, 13.53) * mm});
            skLineSegment(sketch, "E201.1.0.234", {"start": v(33.42, 14.8) * mm, "end": v(30.27, 17.97) * mm});
            skLineSegment(sketch, "E201.1.0.235", {"start": v(33.42, 12.25) * mm, "end": v(30.28, 9.08) * mm});
            skLineSegment(sketch, "E201.1.0.236", {"start": v(83.8, 42.55) * mm, "end": v(86.53, 45.28) * mm});
            skLineSegment(sketch, "E201.1.0.237", {"start": v(52.05, -14.6) * mm, "end": v(49.32, -17.33) * mm});
            skLineSegment(sketch, "E201.1.0.238", {"start": v(87.43, 9) * mm, "end": v(87.43, -17.32) * mm});
            skLineSegment(sketch, "E201.1.0.239", {"start": v(-1.48, 9) * mm, "end": v(-1.47, -17.32) * mm});
            skPoint(sketch, "E201.1.0.240", {"position": v(87.43, 13.53) * mm});
            skLineSegment(sketch, "E201.1.0.241", {"start": v(33.42, 12.25) * mm, "end": v(36.56, 9.08) * mm});
            skLineSegment(sketch, "E201.1.0.242", {"start": v(2.15, 42.55) * mm, "end": v(-0.58, 45.28) * mm});
            skLineSegment(sketch, "E201.1.0.243", {"start": v(83.8, -15.5) * mm, "end": v(86.53, -18.22) * mm});
            skLineSegment(sketch, "E201.1.0.244", {"start": v(2.15, -15.5) * mm, "end": v(-0.58, -18.22) * mm});
            skLineSegment(sketch, "E201.1.0.245", {"start": v(84.7, 41.65) * mm, "end": v(87.43, 44.38) * mm});
            skLineSegment(sketch, "E201.1.0.246", {"start": v(1.25, -14.6) * mm, "end": v(-1.47, -17.32) * mm});
            skLineSegment(sketch, "E201.1.0.247", {"start": v(4.88, 16.7) * mm, "end": v(1.7, 13.53) * mm});
            skLineSegment(sketch, "E201.1.0.248", {"start": v(-1.48, 9) * mm, "end": v(-1.47, -17.32) * mm});
            skLineSegment(sketch, "E201.1.0.249", {"start": v(49.4, 17.97) * mm, "end": v(49.32, 18.04) * mm});
            skLineSegment(sketch, "E201.1.0.250", {"start": v(33.43, 13.54) * mm, "end": v(30.28, 10.35) * mm});
            skLineSegment(sketch, "E201.1.0.251", {"start": v(87.43, -17.32) * mm, "end": v(87.43, 9) * mm});
            skLineSegment(sketch, "E201.1.0.252", {"start": v(52.52, 13.54) * mm, "end": v(55.67, 10.35) * mm});
            skLineSegment(sketch, "E201.1.0.253", {"start": v(30.27, 16.7) * mm, "end": v(33.45, 13.53) * mm});
            skPoint(sketch, "E201.1.0.254", {"position": v(87.43, 13.53) * mm});
            skPoint(sketch, "E201.1.0.255", {"position": v(49.33, 13.53) * mm});
            skPoint(sketch, "E201.1.0.256", {"position": v(-1.47, 13.53) * mm});
            skLineSegment(sketch, "E201.1.0.257", {"start": v(84.23, 13.54) * mm, "end": v(81.08, 10.35) * mm});
            skLineSegment(sketch, "E201.1.0.258", {"start": v(81.08, 16.7) * mm, "end": v(84.25, 13.53) * mm});
            skLineSegment(sketch, "E201.1.0.259", {"start": v(55.68, 16.7) * mm, "end": v(52.5, 13.53) * mm});
            skLineSegment(sketch, "E201.1.0.260", {"start": v(49.4, 9.08) * mm, "end": v(49.32, 9.01) * mm});
            skLineSegment(sketch, "E201.1.0.261", {"start": v(36.56, 17.97) * mm, "end": v(36.63, 18.04) * mm});
            skPoint(sketch, "E201.1.0.262", {"position": v(36.63, 13.53) * mm});
            skLineSegment(sketch, "E201.1.0.263", {"start": v(36.56, 9.08) * mm, "end": v(36.63, 9.01) * mm});
            skPoint(sketch, "E201.1.0.264", {"position": v(49.33, 13.53) * mm});
            skLineSegment(sketch, "E201.1.0.265", {"start": v(-1.4, 17.97) * mm, "end": v(-1.47, 18.04) * mm});
            skPoint(sketch, "E201.1.0.266", {"position": v(-1.47, 13.53) * mm});
            skPoint(sketch, "E201.1.0.267", {"position": v(87.43, 13.53) * mm});
            skLineSegment(sketch, "E201.1.0.268", {"start": v(1.72, 13.54) * mm, "end": v(4.88, 10.35) * mm});
            skPoint(sketch, "E201.1.0.269", {"position": v(36.63, 13.53) * mm});
            skPoint(sketch, "E201.1.0.270", {"position": v(-1.47, 13.53) * mm});
            skPoint(sketch, "E201.1.0.271", {"position": v(36.63, 13.53) * mm});
            skPoint(sketch, "E201.1.0.272", {"position": v(87.43, 13.53) * mm});
            skLineSegment(sketch, "E201.1.0.273", {"start": v(87.36, 17.97) * mm, "end": v(87.43, 18.04) * mm});
            skPoint(sketch, "E201.1.0.274", {"position": v(49.32, 13.53) * mm});
            skPoint(sketch, "E201.1.0.275", {"position": v(-1.47, 13.53) * mm});
            skPoint(sketch, "E201.1.0.276", {"position": v(87.43, 13.53) * mm});
            skPoint(sketch, "E201.1.0.277", {"position": v(36.63, 13.53) * mm});
            skPoint(sketch, "E201.1.0.278", {"position": v(49.32, 13.53) * mm});
            skLineSegment(sketch, "E201.1.0.279", {"start": v(1.7, 13.52) * mm, "end": v(1.7, 13.52) * mm});
            skLineSegment(sketch, "E201.1.0.280", {"start": v(84.25, 13.52) * mm, "end": v(84.25, 13.52) * mm});
            skLineSegment(sketch, "E201.1.0.281", {"start": v(87.36, 9.08) * mm, "end": v(87.43, 9) * mm});
            skLineSegment(sketch, "E201.1.0.282", {"start": v(-1.4, 9.08) * mm, "end": v(-1.48, 9) * mm});
            skLineSegment(sketch, "E201.1.0.283", {"start": v(84.25, 13.52) * mm, "end": v(84.25, 13.53) * mm});
            skLineSegment(sketch, "E201.1.0.284", {"start": v(1.7, 13.53) * mm, "end": v(1.7, 13.52) * mm});
            skLineSegment(sketch, "E201.1.0.285", {"start": v(1.7, 13.52) * mm, "end": v(1.7, 13.53) * mm});
            skLineSegment(sketch, "E201.1.0.286", {"start": v(84.25, 13.53) * mm, "end": v(84.25, 13.52) * mm});
            skLineSegment(sketch, "E201.1.0.287", {"start": v(33.45, 13.56) * mm, "end": v(33.43, 13.54) * mm});
            skLineSegment(sketch, "E201.1.0.288", {"start": v(52.53, 13.53) * mm, "end": v(52.53, 13.56) * mm});
            skLineSegment(sketch, "E201.1.0.289", {"start": v(33.45, 13.56) * mm, "end": v(33.45, 13.53) * mm});
            skLineSegment(sketch, "E201.1.0.290", {"start": v(33.42, 13.53) * mm, "end": v(33.42, 13.56) * mm});
            skLineSegment(sketch, "E201.1.0.291", {"start": v(52.5, 13.56) * mm, "end": v(52.5, 13.53) * mm});
            skLineSegment(sketch, "E201.1.0.292", {"start": v(33.45, 13.53) * mm, "end": v(33.42, 13.53) * mm});
            skLineSegment(sketch, "E201.1.0.293", {"start": v(52.5, 13.53) * mm, "end": v(52.53, 13.53) * mm});
            skLineSegment(sketch, "E201.1.0.294", {"start": v(33.42, 13.53) * mm, "end": v(33.45, 13.53) * mm});
            skLineSegment(sketch, "E201.1.0.295", {"start": v(52.53, 13.53) * mm, "end": v(52.5, 13.53) * mm});
            skLineSegment(sketch, "E201.1.0.296", {"start": v(52.5, 13.56) * mm, "end": v(52.52, 13.54) * mm});
            skPoint(sketch, "E201.2.0.0", {"position": v(106.47, 13.8) * mm});
            skLineSegment(sketch, "E201.2.0.2", {"start": v(144.58, 9.08) * mm, "end": v(144.58, -10.98) * mm});
            skLineSegment(sketch, "E201.2.0.3", {"start": v(144.57, 16.7) * mm, "end": v(119.17, 16.7) * mm});
            skPoint(sketch, "E201.2.0.4", {"position": v(195.38, -11.87) * mm});
            skPoint(sketch, "E201.2.0.6", {"position": v(186.6, -11.87) * mm});
            skPoint(sketch, "E201.2.0.7", {"position": v(166.8, -15.05) * mm});
            skPoint(sketch, "E201.2.0.8", {"position": v(147.75, 10.35) * mm});
            skLineSegment(sketch, "E201.2.0.9", {"start": v(150.03, 45.28) * mm, "end": v(113.72, 45.28) * mm});
            skLineSegment(sketch, "E201.2.0.10", {"start": v(112.83, 44.38) * mm, "end": v(112.83, 18.04) * mm});
            skPoint(sketch, "E201.2.0.11", {"position": v(135.8, -18.22) * mm});
            skPoint(sketch, "E201.2.0.12", {"position": v(150.93, 9.96) * mm});
            skPoint(sketch, "E201.2.0.13", {"position": v(163.62, 9.96) * mm});
            skPoint(sketch, "E201.2.0.14", {"position": v(198.55, -15.05) * mm});
            skLineSegment(sketch, "E201.2.0.15", {"start": v(169.97, 10.35) * mm, "end": v(195.37, 10.35) * mm});
            skPoint(sketch, "E201.2.0.16", {"position": v(195.38, 38.93) * mm});
            skPoint(sketch, "E201.2.0.17", {"position": v(201.73, 45.28) * mm});
            skPoint(sketch, "E201.2.0.19", {"position": v(157.28, -24.57) * mm});
            skLineSegment(sketch, "E201.2.0.20", {"start": v(195.38, 9.08) * mm, "end": v(195.38, -10.97) * mm});
            skPoint(sketch, "E201.2.0.21", {"position": v(147.75, -15.05) * mm});
            skPoint(sketch, "E201.2.0.22", {"position": v(144.26, 16.78) * mm});
            skPoint(sketch, "E201.2.0.23", {"position": v(195.38, 17.1) * mm});
            skPoint(sketch, "E201.2.0.25", {"position": v(163.63, 17.68) * mm});
            skPoint(sketch, "E201.2.0.26", {"position": v(186.6, 38.93) * mm});
            skLineSegment(sketch, "E201.2.0.27", {"start": v(143.68, 38.93) * mm, "end": v(120.07, 38.93) * mm});
            skPoint(sketch, "E201.2.0.28", {"position": v(195.38, 9.96) * mm});
            skLineSegment(sketch, "E201.2.0.29", {"start": v(119.18, 9.08) * mm, "end": v(119.18, -10.97) * mm});
            skPoint(sketch, "E201.2.0.30", {"position": v(169.98, 13.97) * mm});
            skPoint(sketch, "E201.2.0.31", {"position": v(112.83, 17.68) * mm});
            skPoint(sketch, "E201.2.0.32", {"position": v(127.96, 38.93) * mm});
            skLineSegment(sketch, "E201.2.0.34", {"start": v(170.87, 38.93) * mm, "end": v(194.48, 38.93) * mm});
            skLineSegment(sketch, "E201.2.0.35", {"start": v(163.62, 44.38) * mm, "end": v(163.62, 18.04) * mm});
            skLineSegment(sketch, "E201.2.0.36", {"start": v(157.28, 52.19) * mm, "end": v(182.68, 52.19) * mm});
            skLineSegment(sketch, "E201.2.0.37", {"start": v(157.28, -24.01) * mm, "end": v(106.48, -24.01) * mm});
            skPoint(sketch, "E201.2.0.38", {"position": v(150.93, -18.22) * mm});
            skPoint(sketch, "E201.2.0.39", {"position": v(144.58, 12.9) * mm});
            skPoint(sketch, "E201.2.0.40", {"position": v(201.73, 16.77) * mm});
            skPoint(sketch, "E201.2.0.41", {"position": v(144.57, 14.16) * mm});
            skPoint(sketch, "E201.2.0.42", {"position": v(127.96, 45.28) * mm});
            skPoint(sketch, "E201.2.0.43", {"position": v(112.83, 13.53) * mm});
            skPoint(sketch, "E201.2.0.44", {"position": v(178.76, -11.87) * mm});
            skPoint(sketch, "E201.2.0.45", {"position": v(166.8, 42.1) * mm});
            skLineSegment(sketch, "E201.2.0.46", {"start": v(169.97, 9.08) * mm, "end": v(169.97, -10.98) * mm});
            skPoint(sketch, "E201.2.0.47", {"position": v(147.75, 16.7) * mm});
            skPoint(sketch, "E201.2.0.48", {"position": v(112.83, 45.28) * mm});
            skLineSegment(sketch, "E201.2.0.49", {"start": v(208.08, -24.01) * mm, "end": v(157.28, -24.01) * mm});
            skPoint(sketch, "E201.2.0.50", {"position": v(163.62, 45.28) * mm});
            skPoint(sketch, "E201.2.0.51", {"position": v(170.3, 10.28) * mm});
            skLineSegment(sketch, "E201.2.0.52", {"start": v(169.98, 38.03) * mm, "end": v(169.98, 17.97) * mm});
            skLineSegment(sketch, "E201.2.0.53", {"start": v(157.28, 52.19) * mm, "end": v(106.48, 52.19) * mm});
            skPoint(sketch, "E201.2.0.54", {"position": v(208.08, 13.8) * mm});
            skPoint(sketch, "E201.2.0.55", {"position": v(201.73, 13.53) * mm});
            skPoint(sketch, "E201.2.0.56", {"position": v(178.76, 45.28) * mm});
            skPoint(sketch, "E201.2.0.57", {"position": v(119.5, 16.78) * mm});
            skPoint(sketch, "E201.2.0.58", {"position": v(195.06, 10.28) * mm});
            skPoint(sketch, "E201.2.0.59", {"position": v(169.97, 9.96) * mm});
            skPoint(sketch, "E201.2.0.60", {"position": v(186.6, 45.28) * mm});
            skPoint(sketch, "E201.2.0.61", {"position": v(163.62, -18.22) * mm});
            skPoint(sketch, "E201.2.0.62", {"position": v(157.28, 13.8) * mm});
            skPoint(sketch, "E201.2.0.63", {"position": v(169.98, 13.53) * mm});
            skPoint(sketch, "E201.2.0.64", {"position": v(169.98, -11.87) * mm});
            skPoint(sketch, "E201.2.0.65", {"position": v(220.78, 14.09) * mm});
            skPoint(sketch, "E201.2.0.66", {"position": v(208.08, 13.53) * mm});
            skPoint(sketch, "E201.2.0.68", {"position": v(119.18, 12.9) * mm});
            skPoint(sketch, "E201.2.0.69", {"position": v(163.62, 13.53) * mm});
            skPoint(sketch, "E201.2.0.70", {"position": v(214.43, 52.19) * mm});
            skPoint(sketch, "E201.2.0.71", {"position": v(144.58, -11.87) * mm});
            skPoint(sketch, "E201.2.0.72", {"position": v(116, -15.05) * mm});
            skLineSegment(sketch, "E201.2.0.73", {"start": v(201.73, 44.38) * mm, "end": v(201.73, 18.04) * mm});
            skPoint(sketch, "E201.2.0.74", {"position": v(182.68, -24.57) * mm});
            skPoint(sketch, "E201.2.0.75", {"position": v(169.98, 12.9) * mm});
            skPoint(sketch, "E201.2.0.76", {"position": v(163.62, 17.1) * mm});
            skPoint(sketch, "E201.2.0.77", {"position": v(119.18, -11.87) * mm});
            skLineSegment(sketch, "E201.2.0.78", {"start": v(163.62, 9.01) * mm, "end": v(163.62, -17.33) * mm});
            skPoint(sketch, "E201.2.0.79", {"position": v(178.76, 38.93) * mm});
            skLineSegment(sketch, "E201.2.0.80", {"start": v(170.87, -11.87) * mm, "end": v(194.48, -11.87) * mm});
            skLineSegment(sketch, "E201.2.0.81", {"start": v(119.18, 38.03) * mm, "end": v(119.18, 17.97) * mm});
            skPoint(sketch, "E201.2.0.82", {"position": v(116, 42.1) * mm});
            skPoint(sketch, "E201.2.0.83", {"position": v(166.8, 10.35) * mm});
            skPoint(sketch, "E201.2.0.84", {"position": v(163.63, 16.7) * mm});
            skPoint(sketch, "E201.2.0.85", {"position": v(150.93, 17.68) * mm});
            skPoint(sketch, "E201.2.0.86", {"position": v(178.76, -18.22) * mm});
            skPoint(sketch, "E201.2.0.87", {"position": v(195.38, 12.9) * mm});
            skPoint(sketch, "E201.2.0.88", {"position": v(169.98, 38.93) * mm});
            skPoint(sketch, "E201.2.0.89", {"position": v(119.5, 10.28) * mm});
            skPoint(sketch, "E201.2.0.90", {"position": v(150.93, 13.53) * mm});
            skPoint(sketch, "E201.2.0.91", {"position": v(208.08, -24.57) * mm});
            skLineSegment(sketch, "E201.2.0.92", {"start": v(164.52, 45.28) * mm, "end": v(200.83, 45.28) * mm});
            skLineSegment(sketch, "E201.2.0.93", {"start": v(164.52, -18.22) * mm, "end": v(200.83, -18.22) * mm});
            skPoint(sketch, "E201.2.0.94", {"position": v(144.58, 9.96) * mm});
            skPoint(sketch, "E201.2.0.95", {"position": v(144.26, 10.28) * mm});
            skLineSegment(sketch, "E201.2.0.96", {"start": v(144.57, 38.03) * mm, "end": v(144.57, 17.97) * mm});
            skLineSegment(sketch, "E201.2.0.97", {"start": v(144.58, 10.35) * mm, "end": v(119.18, 10.35) * mm});
            skPoint(sketch, "E201.2.0.98", {"position": v(201.73, -18.22) * mm});
            skPoint(sketch, "E201.2.0.99", {"position": v(166.8, 16.7) * mm});
            skPoint(sketch, "E201.2.0.100", {"position": v(144.57, 38.93) * mm});
            skLineSegment(sketch, "E201.2.0.101", {"start": v(112.83, -17.32) * mm, "end": v(112.82, 9) * mm});
            skPoint(sketch, "E201.2.0.102", {"position": v(150.93, 45.28) * mm});
            skPoint(sketch, "E201.2.0.103", {"position": v(119.18, 17.1) * mm});
            skPoint(sketch, "E201.2.0.104", {"position": v(119.18, 9.96) * mm});
            skLineSegment(sketch, "E201.2.0.105", {"start": v(182.68, 52.19) * mm, "end": v(208.08, 52.19) * mm});
            skLineSegment(sketch, "E201.2.0.106", {"start": v(143.68, -11.87) * mm, "end": v(120.07, -11.87) * mm});
            skPoint(sketch, "E201.2.0.107", {"position": v(127.96, -11.87) * mm});
            skPoint(sketch, "E201.2.0.108", {"position": v(208.08, 51.63) * mm});
            skPoint(sketch, "E201.2.0.109", {"position": v(106.48, 13.53) * mm});
            skLineSegment(sketch, "E201.2.0.110", {"start": v(150.03, -18.22) * mm, "end": v(113.72, -18.22) * mm});
            skPoint(sketch, "E201.2.0.111", {"position": v(119.18, 38.93) * mm});
            skPoint(sketch, "E201.2.0.112", {"position": v(135.8, -11.87) * mm});
            skLineSegment(sketch, "E201.2.0.113", {"start": v(150.93, 44.38) * mm, "end": v(150.93, 18.04) * mm});
            skPoint(sketch, "E201.2.0.115", {"position": v(135.8, 45.28) * mm});
            skLineSegment(sketch, "E201.2.0.116", {"start": v(150.93, -17.33) * mm, "end": v(150.93, 9.01) * mm});
            skPoint(sketch, "E201.2.0.117", {"position": v(135.8, 38.93) * mm});
            skLineSegment(sketch, "E201.2.0.118", {"start": v(169.98, 16.7) * mm, "end": v(195.38, 16.7) * mm});
            skPoint(sketch, "E201.2.0.119", {"position": v(127.96, -18.22) * mm});
            skPoint(sketch, "E201.2.0.120", {"position": v(147.75, 42.1) * mm});
            skPoint(sketch, "E201.2.0.121", {"position": v(198.55, 42.1) * mm});
            skPoint(sketch, "E201.2.0.122", {"position": v(186.6, -18.22) * mm});
            skPoint(sketch, "E201.2.0.123", {"position": v(170.3, 16.78) * mm});
            skPoint(sketch, "E201.2.0.124", {"position": v(214.43, -24.01) * mm});
            skPoint(sketch, "E201.2.0.125", {"position": v(195.06, 16.78) * mm});
            skPoint(sketch, "E201.2.0.126", {"position": v(112.83, -18.22) * mm});
            skLineSegment(sketch, "E201.2.0.127", {"start": v(195.38, 38.03) * mm, "end": v(195.38, 17.97) * mm});
            skPoint(sketch, "E201.2.0.128", {"position": v(112.82, 16.77) * mm});
            skLineSegment(sketch, "E201.2.0.129", {"start": v(201.73, -17.5) * mm, "end": v(201.73, 9) * mm});
            skPoint(sketch, "E201.2.0.130", {"position": v(150.92, 16.7) * mm});
            skLineSegment(sketch, "E201.2.0.131", {"start": v(170.87, -11.87) * mm, "end": v(194.48, -11.87) * mm});
            skLineSegment(sketch, "E201.2.0.132", {"start": v(119.18, 9.08) * mm, "end": v(119.18, -10.97) * mm});
            skPoint(sketch, "E201.2.0.133", {"position": v(169.98, 14.16) * mm});
            skPoint(sketch, "E201.2.0.134", {"position": v(163.63, -18.22) * mm});
            skPoint(sketch, "E201.2.0.135", {"position": v(119.18, 12.9) * mm});
            skPoint(sketch, "E201.2.0.136", {"position": v(150.93, 17.1) * mm});
            skLineSegment(sketch, "E201.2.0.137", {"start": v(195.38, 9.08) * mm, "end": v(195.38, -10.97) * mm});
            skLineSegment(sketch, "E201.2.0.138", {"start": v(150.93, 9.01) * mm, "end": v(150.93, -17.33) * mm});
            skLineSegment(sketch, "E201.2.0.139", {"start": v(147.3, 42.55) * mm, "end": v(143.68, 38.93) * mm});
            skPoint(sketch, "E201.2.0.140", {"position": v(112.83, 45.28) * mm});
            skLineSegment(sketch, "E201.2.0.141", {"start": v(166.35, -14.6) * mm, "end": v(169.97, -10.98) * mm});
            skLineSegment(sketch, "E201.2.0.142", {"start": v(115.55, 41.65) * mm, "end": v(119.18, 38.03) * mm});
            skLineSegment(sketch, "E201.2.0.143", {"start": v(199, -14.6) * mm, "end": v(195.38, -10.97) * mm});
            skLineSegment(sketch, "E201.2.0.144", {"start": v(167.25, -15.5) * mm, "end": v(170.87, -11.87) * mm});
            skPoint(sketch, "E201.2.0.145", {"position": v(119.5, 10.28) * mm});
            skPoint(sketch, "E201.2.0.146", {"position": v(195.38, 14.16) * mm});
            skPoint(sketch, "E201.2.0.147", {"position": v(170.3, 10.28) * mm});
            skPoint(sketch, "E201.2.0.148", {"position": v(163.63, 16.77) * mm});
            skPoint(sketch, "E201.2.0.149", {"position": v(201.73, 45.28) * mm});
            skPoint(sketch, "E201.2.0.150", {"position": v(201.73, 13.53) * mm});
            skPoint(sketch, "E201.2.0.151", {"position": v(169.98, 12.9) * mm});
            skPoint(sketch, "E201.2.0.152", {"position": v(208.08, -24.57) * mm});
            skPoint(sketch, "E201.2.0.153", {"position": v(119.18, 14.16) * mm});
            skLineSegment(sketch, "E201.2.0.154", {"start": v(148.2, -14.6) * mm, "end": v(144.58, -10.98) * mm});
            skLineSegment(sketch, "E201.2.0.155", {"start": v(143.68, -11.87) * mm, "end": v(120.07, -11.87) * mm});
            skPoint(sketch, "E201.2.0.156", {"position": v(201.73, -18.22) * mm});
            skPoint(sketch, "E201.2.0.157", {"position": v(119.5, 16.78) * mm});
            skPoint(sketch, "E201.2.0.158", {"position": v(201.73, 16.7) * mm});
            skLineSegment(sketch, "E201.2.0.159", {"start": v(147.3, -15.5) * mm, "end": v(143.68, -11.87) * mm});
            skLineSegment(sketch, "E201.2.0.160", {"start": v(198.1, -15.5) * mm, "end": v(194.48, -11.87) * mm});
            skLineSegment(sketch, "E201.2.0.161", {"start": v(112.82, 9) * mm, "end": v(112.83, -17.32) * mm});
            skLineSegment(sketch, "E201.2.0.162", {"start": v(167.25, 42.55) * mm, "end": v(170.87, 38.93) * mm});
            skLineSegment(sketch, "E201.2.0.163", {"start": v(201.73, 44.38) * mm, "end": v(201.73, 18.04) * mm});
            skLineSegment(sketch, "E201.2.0.164", {"start": v(148.2, 41.65) * mm, "end": v(144.57, 38.03) * mm});
            skPoint(sketch, "E201.2.0.165", {"position": v(163.63, 13.53) * mm});
            skLineSegment(sketch, "E201.2.0.166", {"start": v(198.1, 42.55) * mm, "end": v(194.48, 38.93) * mm});
            skLineSegment(sketch, "E201.2.0.167", {"start": v(166.35, 41.65) * mm, "end": v(169.98, 38.03) * mm});
            skLineSegment(sketch, "E201.2.0.168", {"start": v(119.18, 38.03) * mm, "end": v(119.18, 17.97) * mm});
            skPoint(sketch, "E201.2.0.169", {"position": v(195.06, 16.78) * mm});
            skLineSegment(sketch, "E201.2.0.170", {"start": v(201.73, 9) * mm, "end": v(201.73, -17.32) * mm});
            skLineSegment(sketch, "E201.2.0.171", {"start": v(164.52, -18.22) * mm, "end": v(200.83, -18.22) * mm});
            skPoint(sketch, "E201.2.0.172", {"position": v(112.83, 13.53) * mm});
            skLineSegment(sketch, "E201.2.0.173", {"start": v(112.83, 44.38) * mm, "end": v(112.83, 18.04) * mm});
            skPoint(sketch, "E201.2.0.174", {"position": v(195.38, 12.9) * mm});
            skLineSegment(sketch, "E201.2.0.175", {"start": v(199, 41.65) * mm, "end": v(195.38, 38.03) * mm});
            skPoint(sketch, "E201.2.0.176", {"position": v(144.58, 13.97) * mm});
            skPoint(sketch, "E201.2.0.177", {"position": v(195.06, 10.28) * mm});
            skPoint(sketch, "E201.2.0.178", {"position": v(144.58, 12.9) * mm});
            skLineSegment(sketch, "E201.2.0.179", {"start": v(116.45, -15.5) * mm, "end": v(120.07, -11.87) * mm});
            skPoint(sketch, "E201.2.0.180", {"position": v(144.26, 10.28) * mm});
            skPoint(sketch, "E201.2.0.181", {"position": v(112.82, 16.7) * mm});
            skLineSegment(sketch, "E201.2.0.182", {"start": v(116.45, 42.55) * mm, "end": v(120.07, 38.93) * mm});
            skPoint(sketch, "E201.2.0.183", {"position": v(150.93, 13.53) * mm});
            skLineSegment(sketch, "E201.2.0.184", {"start": v(195.38, 38.03) * mm, "end": v(195.38, 17.97) * mm});
            skPoint(sketch, "E201.2.0.185", {"position": v(170.3, 16.78) * mm});
            skLineSegment(sketch, "E201.2.0.186", {"start": v(163.62, -17.33) * mm, "end": v(163.62, 9.01) * mm});
            skLineSegment(sketch, "E201.2.0.187", {"start": v(115.55, -14.6) * mm, "end": v(119.18, -10.97) * mm});
            skLineSegment(sketch, "E201.2.0.188", {"start": v(150.03, -18.22) * mm, "end": v(113.72, -18.22) * mm});
            skPoint(sketch, "E201.2.0.189", {"position": v(144.26, 16.78) * mm});
            skPoint(sketch, "E201.2.0.190", {"position": v(201.73, 17.68) * mm});
            skPoint(sketch, "E201.2.0.191", {"position": v(112.83, -18.22) * mm});
            skPoint(sketch, "E201.2.0.192", {"position": v(150.93, -18.22) * mm});
            skLineSegment(sketch, "E201.2.0.193", {"start": v(201.73, 44.38) * mm, "end": v(201.73, 18.04) * mm});
            skLineSegment(sketch, "E201.2.0.194", {"start": v(147.3, 42.55) * mm, "end": v(150.03, 45.28) * mm});
            skPoint(sketch, "E201.2.0.195", {"position": v(119.18, 13.53) * mm});
            skPoint(sketch, "E201.2.0.196", {"position": v(144.58, 13.53) * mm});
            skLineSegment(sketch, "E201.2.0.197", {"start": v(116.03, 14.8) * mm, "end": v(112.9, 17.97) * mm});
            skLineSegment(sketch, "E201.2.0.198", {"start": v(116.03, 12.26) * mm, "end": v(119.18, 9.08) * mm});
            skPoint(sketch, "E201.2.0.199", {"position": v(150.93, 16.77) * mm});
            skLineSegment(sketch, "E201.2.0.200", {"start": v(195.38, 38.03) * mm, "end": v(195.38, 17.97) * mm});
            skLineSegment(sketch, "E201.2.0.201", {"start": v(119.18, 9.08) * mm, "end": v(119.18, -10.97) * mm});
            skLineSegment(sketch, "E201.2.0.202", {"start": v(148.2, 41.65) * mm, "end": v(150.93, 44.38) * mm});
            skLineSegment(sketch, "E201.2.0.203", {"start": v(116.03, 12.26) * mm, "end": v(112.9, 9.08) * mm});
            skPoint(sketch, "E201.2.0.204", {"position": v(112.83, 13.53) * mm});
            skPoint(sketch, "E201.2.0.205", {"position": v(163.63, 13.53) * mm});
            skLineSegment(sketch, "E201.2.0.206", {"start": v(119.18, 38.03) * mm, "end": v(119.18, 17.97) * mm});
            skLineSegment(sketch, "E201.2.0.207", {"start": v(112.83, 44.38) * mm, "end": v(112.83, 18.04) * mm});
            skLineSegment(sketch, "E201.2.0.208", {"start": v(166.35, 41.65) * mm, "end": v(163.62, 44.38) * mm});
            skLineSegment(sketch, "E201.2.0.209", {"start": v(167.25, 42.55) * mm, "end": v(164.52, 45.28) * mm});
            skPoint(sketch, "E201.2.0.210", {"position": v(150.93, 13.53) * mm});
            skLineSegment(sketch, "E201.2.0.211", {"start": v(198.52, 12.26) * mm, "end": v(195.38, 9.08) * mm});
            skLineSegment(sketch, "E201.2.0.212", {"start": v(166.83, 12.25) * mm, "end": v(169.97, 9.08) * mm});
            skLineSegment(sketch, "E201.2.0.213", {"start": v(116.03, 14.8) * mm, "end": v(119.18, 17.97) * mm});
            skLineSegment(sketch, "E201.2.0.214", {"start": v(112.83, -17.5) * mm, "end": v(112.82, 9) * mm});
            skLineSegment(sketch, "E201.2.0.215", {"start": v(195.38, 9.08) * mm, "end": v(195.38, -10.97) * mm});
            skLineSegment(sketch, "E201.2.0.216", {"start": v(201.73, 9) * mm, "end": v(201.73, -17.32) * mm});
            skPoint(sketch, "E201.2.0.217", {"position": v(195.38, 13.53) * mm});
            skPoint(sketch, "E201.2.0.218", {"position": v(201.73, 13.53) * mm});
            skLineSegment(sketch, "E201.2.0.219", {"start": v(198.52, 12.26) * mm, "end": v(201.66, 9.08) * mm});
            skLineSegment(sketch, "E201.2.0.220", {"start": v(166.83, 12.25) * mm, "end": v(163.7, 9.08) * mm});
            skLineSegment(sketch, "E201.2.0.221", {"start": v(199, -14.6) * mm, "end": v(201.73, -17.32) * mm});
            skLineSegment(sketch, "E201.2.0.222", {"start": v(147.3, -15.5) * mm, "end": v(150.03, -18.22) * mm});
            skLineSegment(sketch, "E201.2.0.223", {"start": v(115.55, 41.65) * mm, "end": v(112.83, 44.38) * mm});
            skPoint(sketch, "E201.2.0.224", {"position": v(150.93, 13.53) * mm});
            skLineSegment(sketch, "E201.2.0.225", {"start": v(198.52, 14.8) * mm, "end": v(195.38, 17.97) * mm});
            skLineSegment(sketch, "E201.2.0.226", {"start": v(148.2, -14.6) * mm, "end": v(150.93, -17.33) * mm});
            skPoint(sketch, "E201.2.0.227", {"position": v(112.83, 13.53) * mm});
            skLineSegment(sketch, "E201.2.0.228", {"start": v(166.83, 14.8) * mm, "end": v(163.7, 17.97) * mm});
            skLineSegment(sketch, "E201.2.0.229", {"start": v(166.83, 14.8) * mm, "end": v(169.98, 17.97) * mm});
            skLineSegment(sketch, "E201.2.0.230", {"start": v(147.72, 14.8) * mm, "end": v(150.86, 17.97) * mm});
            skLineSegment(sketch, "E201.2.0.231", {"start": v(198.52, 14.8) * mm, "end": v(201.66, 17.97) * mm});
            skLineSegment(sketch, "E201.2.0.232", {"start": v(167.25, -15.5) * mm, "end": v(164.52, -18.22) * mm});
            skPoint(sketch, "E201.2.0.233", {"position": v(163.63, 13.53) * mm});
            skLineSegment(sketch, "E201.2.0.234", {"start": v(147.72, 14.8) * mm, "end": v(144.57, 17.97) * mm});
            skLineSegment(sketch, "E201.2.0.235", {"start": v(147.72, 12.25) * mm, "end": v(144.58, 9.08) * mm});
            skLineSegment(sketch, "E201.2.0.236", {"start": v(198.1, 42.55) * mm, "end": v(200.83, 45.28) * mm});
            skLineSegment(sketch, "E201.2.0.237", {"start": v(166.35, -14.6) * mm, "end": v(163.62, -17.33) * mm});
            skLineSegment(sketch, "E201.2.0.238", {"start": v(201.73, 9) * mm, "end": v(201.73, -17.32) * mm});
            skLineSegment(sketch, "E201.2.0.239", {"start": v(112.82, 9) * mm, "end": v(112.83, -17.32) * mm});
            skPoint(sketch, "E201.2.0.240", {"position": v(201.73, 13.53) * mm});
            skLineSegment(sketch, "E201.2.0.241", {"start": v(147.72, 12.25) * mm, "end": v(150.86, 9.08) * mm});
            skLineSegment(sketch, "E201.2.0.242", {"start": v(116.45, 42.55) * mm, "end": v(113.72, 45.28) * mm});
            skLineSegment(sketch, "E201.2.0.243", {"start": v(198.1, -15.5) * mm, "end": v(200.83, -18.22) * mm});
            skLineSegment(sketch, "E201.2.0.244", {"start": v(116.45, -15.5) * mm, "end": v(113.72, -18.22) * mm});
            skLineSegment(sketch, "E201.2.0.245", {"start": v(199, 41.65) * mm, "end": v(201.73, 44.38) * mm});
            skLineSegment(sketch, "E201.2.0.246", {"start": v(115.55, -14.6) * mm, "end": v(112.83, -17.32) * mm});
            skLineSegment(sketch, "E201.2.0.247", {"start": v(119.18, 16.7) * mm, "end": v(116, 13.53) * mm});
            skLineSegment(sketch, "E201.2.0.248", {"start": v(112.82, 9) * mm, "end": v(112.83, -17.32) * mm});
            skLineSegment(sketch, "E201.2.0.249", {"start": v(163.7, 17.97) * mm, "end": v(163.62, 18.04) * mm});
            skLineSegment(sketch, "E201.2.0.250", {"start": v(147.73, 13.54) * mm, "end": v(144.58, 10.35) * mm});
            skLineSegment(sketch, "E201.2.0.251", {"start": v(201.73, -17.32) * mm, "end": v(201.73, 9) * mm});
            skLineSegment(sketch, "E201.2.0.252", {"start": v(166.82, 13.54) * mm, "end": v(169.97, 10.35) * mm});
            skLineSegment(sketch, "E201.2.0.253", {"start": v(144.57, 16.7) * mm, "end": v(147.75, 13.53) * mm});
            skPoint(sketch, "E201.2.0.254", {"position": v(201.73, 13.53) * mm});
            skPoint(sketch, "E201.2.0.255", {"position": v(163.63, 13.53) * mm});
            skPoint(sketch, "E201.2.0.256", {"position": v(112.83, 13.53) * mm});
            skLineSegment(sketch, "E201.2.0.257", {"start": v(198.53, 13.54) * mm, "end": v(195.38, 10.35) * mm});
            skLineSegment(sketch, "E201.2.0.258", {"start": v(195.38, 16.7) * mm, "end": v(198.55, 13.53) * mm});
            skLineSegment(sketch, "E201.2.0.259", {"start": v(169.98, 16.7) * mm, "end": v(166.8, 13.53) * mm});
            skLineSegment(sketch, "E201.2.0.260", {"start": v(163.7, 9.08) * mm, "end": v(163.62, 9.01) * mm});
            skLineSegment(sketch, "E201.2.0.261", {"start": v(150.86, 17.97) * mm, "end": v(150.93, 18.04) * mm});
            skPoint(sketch, "E201.2.0.262", {"position": v(150.93, 13.53) * mm});
            skLineSegment(sketch, "E201.2.0.263", {"start": v(150.86, 9.08) * mm, "end": v(150.93, 9.01) * mm});
            skPoint(sketch, "E201.2.0.264", {"position": v(163.63, 13.53) * mm});
            skLineSegment(sketch, "E201.2.0.265", {"start": v(112.9, 17.97) * mm, "end": v(112.83, 18.04) * mm});
            skPoint(sketch, "E201.2.0.266", {"position": v(112.83, 13.53) * mm});
            skPoint(sketch, "E201.2.0.267", {"position": v(201.73, 13.53) * mm});
            skLineSegment(sketch, "E201.2.0.268", {"start": v(116.02, 13.54) * mm, "end": v(119.18, 10.35) * mm});
            skPoint(sketch, "E201.2.0.269", {"position": v(150.93, 13.53) * mm});
            skPoint(sketch, "E201.2.0.270", {"position": v(112.83, 13.53) * mm});
            skPoint(sketch, "E201.2.0.271", {"position": v(150.93, 13.53) * mm});
            skPoint(sketch, "E201.2.0.272", {"position": v(201.73, 13.53) * mm});
            skLineSegment(sketch, "E201.2.0.273", {"start": v(201.66, 17.97) * mm, "end": v(201.73, 18.04) * mm});
            skPoint(sketch, "E201.2.0.274", {"position": v(163.62, 13.53) * mm});
            skPoint(sketch, "E201.2.0.275", {"position": v(112.83, 13.53) * mm});
            skPoint(sketch, "E201.2.0.276", {"position": v(201.73, 13.53) * mm});
            skPoint(sketch, "E201.2.0.277", {"position": v(150.93, 13.53) * mm});
            skPoint(sketch, "E201.2.0.278", {"position": v(163.62, 13.53) * mm});
            skLineSegment(sketch, "E201.2.0.279", {"start": v(116, 13.52) * mm, "end": v(116, 13.52) * mm});
            skLineSegment(sketch, "E201.2.0.280", {"start": v(198.55, 13.52) * mm, "end": v(198.55, 13.52) * mm});
            skLineSegment(sketch, "E201.2.0.281", {"start": v(201.66, 9.08) * mm, "end": v(201.73, 9) * mm});
            skLineSegment(sketch, "E201.2.0.282", {"start": v(112.9, 9.08) * mm, "end": v(112.82, 9) * mm});
            skLineSegment(sketch, "E201.2.0.283", {"start": v(198.55, 13.52) * mm, "end": v(198.55, 13.53) * mm});
            skLineSegment(sketch, "E201.2.0.284", {"start": v(116, 13.53) * mm, "end": v(116, 13.52) * mm});
            skLineSegment(sketch, "E201.2.0.285", {"start": v(116, 13.52) * mm, "end": v(116, 13.53) * mm});
            skLineSegment(sketch, "E201.2.0.286", {"start": v(198.55, 13.53) * mm, "end": v(198.55, 13.52) * mm});
            skLineSegment(sketch, "E201.2.0.287", {"start": v(147.75, 13.56) * mm, "end": v(147.73, 13.54) * mm});
            skLineSegment(sketch, "E201.2.0.288", {"start": v(166.83, 13.53) * mm, "end": v(166.83, 13.56) * mm});
            skLineSegment(sketch, "E201.2.0.289", {"start": v(147.75, 13.56) * mm, "end": v(147.75, 13.53) * mm});
            skLineSegment(sketch, "E201.2.0.290", {"start": v(147.72, 13.53) * mm, "end": v(147.72, 13.56) * mm});
            skLineSegment(sketch, "E201.2.0.291", {"start": v(166.8, 13.56) * mm, "end": v(166.8, 13.53) * mm});
            skLineSegment(sketch, "E201.2.0.292", {"start": v(147.75, 13.53) * mm, "end": v(147.72, 13.53) * mm});
            skLineSegment(sketch, "E201.2.0.293", {"start": v(166.8, 13.53) * mm, "end": v(166.83, 13.53) * mm});
            skLineSegment(sketch, "E201.2.0.294", {"start": v(147.72, 13.53) * mm, "end": v(147.75, 13.53) * mm});
            skLineSegment(sketch, "E201.2.0.295", {"start": v(166.83, 13.53) * mm, "end": v(166.8, 13.53) * mm});
            skLineSegment(sketch, "E201.2.0.296", {"start": v(166.8, 13.56) * mm, "end": v(166.82, 13.54) * mm});
            skLineSegment(sketch, "E201.direction1", {"start": v(-122.12, -24.01) * mm, "end": v(-7.82, -24.01) * mm, "construction": true});
            skLineSegment(sketch, "E202", {"start": v(208.08, 52.19) * mm, "end": v(208.08, -24.01) * mm});
            skPoint(sketch, "E203.orphan", {"position": v(220.78, -24.01) * mm});
            skLineSegment(sketch, "E204", {"start": v(-61.78, 13.54) * mm, "end": v(-61.78, 13.54) * mm});
            skPoint(sketch, "E205.trimOffspring.end.orphan", {"position": v(-61.8, 13.53) * mm});
            skLineSegment(sketch, "E206", {"start": v(-109.42, 10.35) * mm, "end": v(-109.42, 10.35) * mm});
            skLineSegment(sketch, "E207", {"start": v(-33.22, 10.35) * mm, "end": v(-33.23, 10.35) * mm});
            skLineSegment(sketch, "E208", {"start": v(4.88, 10.35) * mm, "end": v(4.88, 10.35) * mm});
            skLineSegment(sketch, "E209", {"start": v(81.08, 10.35) * mm, "end": v(81.07, 10.35) * mm});
            skLineSegment(sketch, "E210", {"start": v(119.18, 10.35) * mm, "end": v(119.18, 10.35) * mm});
            skLineSegment(sketch, "E211", {"start": v(195.38, 10.35) * mm, "end": v(195.37, 10.35) * mm});
            skSolve(sketch);
        }
        {
            var Q0;
            Q0=makeQuery(id+"F0.imprint","IMPRINT",FACE,{"disambiguationData":[TD([[makeQuery(id+"F0.imprint","IMPRINT",EDGE,{"derivedFrom":sQuery(id+"F0.wireOp",EDGE,"E0.bottom")}),-1.0]])]});
            extrude(context, id + "F1", {"entities" : qUnion([Q0]), "depth" : 25.4 * mm});
        }
    });
